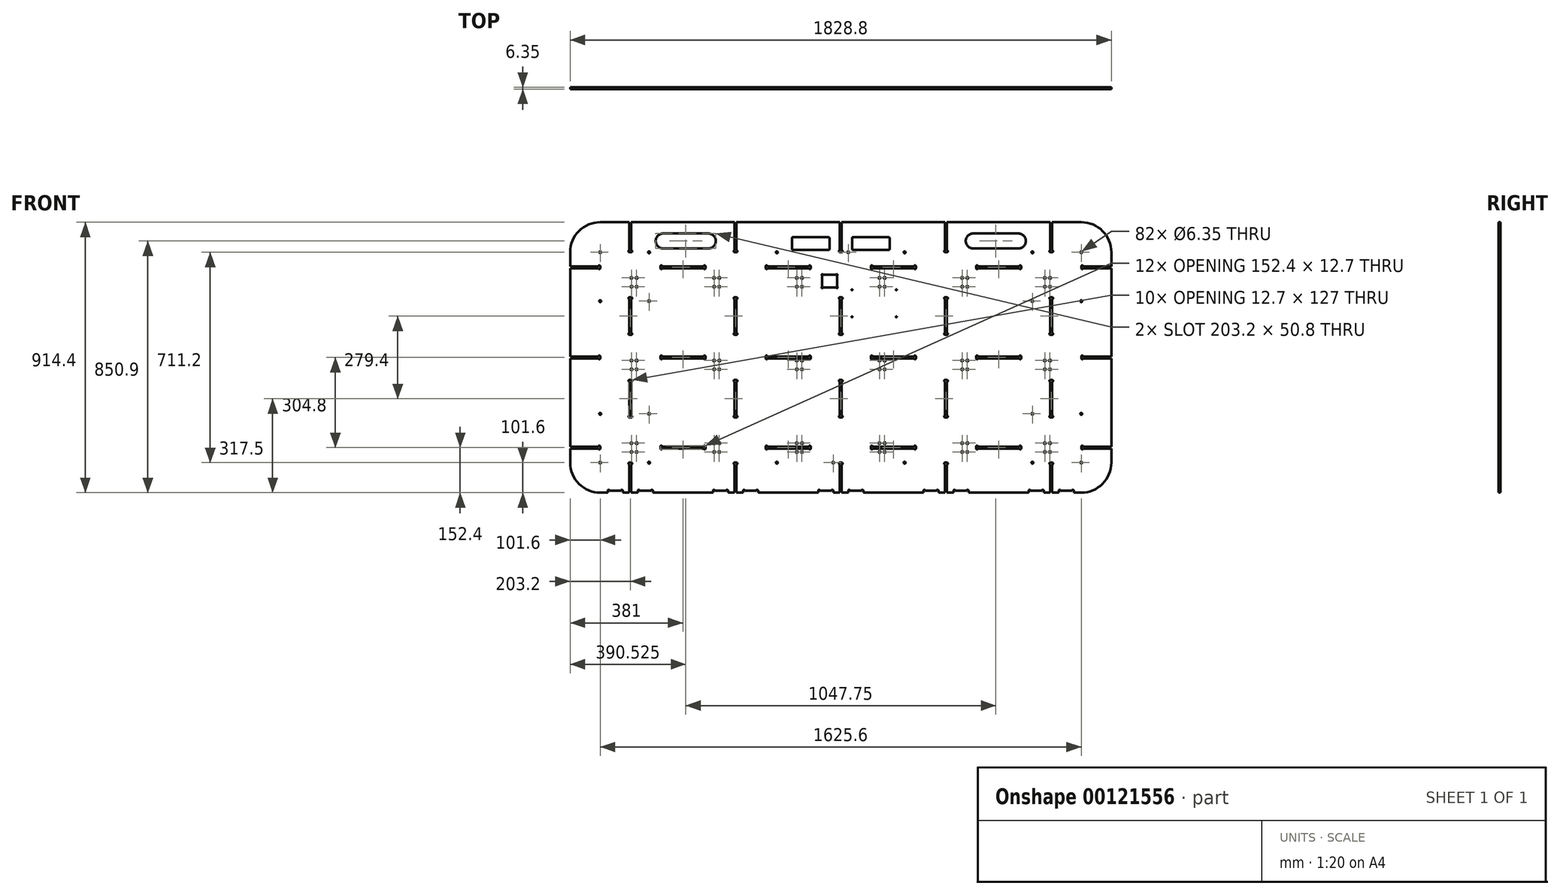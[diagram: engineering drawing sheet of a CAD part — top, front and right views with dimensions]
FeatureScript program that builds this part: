
annotation { "Feature Type Name" : "Feature", "Feature Type Description" : "" }
export const myFeature = defineFeature(function(context is Context, id is Id, definition is map)
    precondition{}
    {
        {
            var Q0;
            Q0=qCreatedBy(makeId("Front.planeOp"),FACE);
            var sketch = newSketch(context, id + "F0", { "sketchPlane" : qUnion([Q0])});
            skLineSegment(sketch, "E0.bottom", {"start": v(-812.8, 0) * mm, "end": v(812.8, 0) * mm});
            skLineSegment(sketch, "E0.top", {"start": v(-812.8, 914.4) * mm, "end": v(812.8, 914.4) * mm});
            skLineSegment(sketch, "E0.left", {"start": v(-914.4, 101.6) * mm, "end": v(-914.4, 812.8) * mm});
            skLineSegment(sketch, "E0.right", {"start": v(914.4, 101.6) * mm, "end": v(914.4, 812.8) * mm});
            skPoint(sketch, "E1.visualSharp", {"position": v(-914.4, 914.4) * mm});
            skArc(sketch, "E1.filletArc", {"start": v(-812.8, 914.4) * mm, "mid": v(-884.64, 884.64) * mm, "end": v(-914.4, 812.8) * mm});
            skPoint(sketch, "E2.visualSharp", {"position": v(-914.4, 0) * mm});
            skArc(sketch, "E2.filletArc", {"start": v(-914.4, 101.6) * mm, "mid": v(-884.64, 29.76) * mm, "end": v(-812.8, 0) * mm});
            skPoint(sketch, "E3.visualSharp", {"position": v(914.4, 0) * mm});
            skArc(sketch, "E3.filletArc", {"start": v(812.8, 0) * mm, "mid": v(884.64, 29.76) * mm, "end": v(914.4, 101.6) * mm});
            skPoint(sketch, "E4.visualSharp", {"position": v(914.4, 914.4) * mm});
            skArc(sketch, "E4.filletArc", {"start": v(914.4, 812.8) * mm, "mid": v(884.64, 884.64) * mm, "end": v(812.8, 914.4) * mm});
            skSolve(sketch);
        }
        {
            var Q0;
            Q0 = qSketchRegion(id + "F0", true);
            extrude(context, id + "F1", {"entities" : qUnion([Q0]), "depth" : 6.35 * mm});
        }
        {
            var Q0;
            Q0=makeQuery(id+"F1.opExtrude","CAP_FACE",FACE,{"disambiguationData":[OSD([sQuery(id+"F0.wireOp",EDGE,"E0.bottom"),sQuery(id+"F0.wireOp",EDGE,"E0.top"),sQuery(id+"F0.wireOp",EDGE,"E0.left"),sQuery(id+"F0.wireOp",EDGE,"E0.right"),sQuery(id+"F0.wireOp",EDGE,"E1.filletArc"),sQuery(id+"F0.wireOp",EDGE,"E2.filletArc"),sQuery(id+"F0.wireOp",EDGE,"E3.filletArc"),sQuery(id+"F0.wireOp",EDGE,"E4.filletArc")])],"isStart":false});
            var sketch = newSketch(context, id + "F2", { "sketchPlane" : qUnion([Q0])});
            skLineSegment(sketch, "E5", {"start": v(-711.2, 0) * mm, "end": v(-711.2, 914.4) * mm, "construction": true});
            skLineSegment(sketch, "E6", {"start": v(-711.2, 914.4) * mm, "end": v(-355.6, 914.4) * mm, "construction": true});
            skLineSegment(sketch, "E7", {"start": v(-355.6, 914.4) * mm, "end": v(-355.6, 0) * mm, "construction": true});
            skLineSegment(sketch, "E8", {"start": v(-355.6, 0) * mm, "end": v(0, 0) * mm, "construction": true});
            skLineSegment(sketch, "E9", {"start": v(0, 0) * mm, "end": v(0, 914.4) * mm, "construction": true});
            skPoint(sketch, "E9.endSnap0", {"position": v(0, 914.4) * mm});
            skLineSegment(sketch, "E10", {"start": v(0, 914.4) * mm, "end": v(355.6, 914.4) * mm, "construction": true});
            skLineSegment(sketch, "E11", {"start": v(355.6, 914.4) * mm, "end": v(355.6, 0) * mm, "construction": true});
            skLineSegment(sketch, "E12", {"start": v(355.6, 0) * mm, "end": v(711.2, 0) * mm, "construction": true});
            skLineSegment(sketch, "E13", {"start": v(711.2, 0) * mm, "end": v(711.2, 914.4) * mm, "construction": true});
            skLineSegment(sketch, "E14", {"start": v(-914.4, 762) * mm, "end": v(914.4, 762) * mm, "construction": true});
            skLineSegment(sketch, "E15", {"start": v(914.4, 762) * mm, "end": v(914.4, 457.2) * mm, "construction": true});
            skLineSegment(sketch, "E16", {"start": v(914.4, 457.2) * mm, "end": v(-914.4, 457.2) * mm, "construction": true});
            skLineSegment(sketch, "E17", {"start": v(-914.4, 457.2) * mm, "end": v(-914.4, 152.4) * mm, "construction": true});
            skLineSegment(sketch, "E18", {"start": v(-914.4, 152.4) * mm, "end": v(914.4, 152.4) * mm, "construction": true});
            skLineSegment(sketch, "E19", {"start": v(-714.38, 933.45) * mm, "end": v(-714.38, 933.45) * mm});
            skLineSegment(sketch, "E20", {"start": v(-714.38, 933.45) * mm, "end": v(-714.38, 819.15) * mm});
            skLineSegment(sketch, "E21", {"start": v(-714.38, 819.15) * mm, "end": v(-714.38, 819.15) * mm});
            skLineSegment(sketch, "E22", {"start": v(-714.38, 812.8) * mm, "end": v(-708.03, 812.8) * mm});
            skLineSegment(sketch, "E23", {"start": v(-708.03, 819.15) * mm, "end": v(-708.03, 819.15) * mm});
            skLineSegment(sketch, "E24", {"start": v(-708.03, 819.15) * mm, "end": v(-708.03, 933.45) * mm});
            skLineSegment(sketch, "E25", {"start": v(-708.03, 933.45) * mm, "end": v(-708.03, 933.45) * mm});
            skLineSegment(sketch, "E26", {"start": v(-708.03, 939.8) * mm, "end": v(-714.37, 939.8) * mm});
            skArc(sketch, "E27", {"start": v(-708.03, 939.8) * mm, "mid": v(-704.85, 936.63) * mm, "end": v(-708.03, 933.45) * mm});
            skArc(sketch, "E28", {"start": v(-714.37, 939.8) * mm, "mid": v(-717.55, 936.63) * mm, "end": v(-714.38, 933.45) * mm});
            skArc(sketch, "E29", {"start": v(-714.38, 819.15) * mm, "mid": v(-717.55, 815.97) * mm, "end": v(-714.38, 812.8) * mm});
            skArc(sketch, "E30", {"start": v(-708.03, 819.15) * mm, "mid": v(-704.85, 815.97) * mm, "end": v(-708.03, 812.8) * mm});
            skLineSegment(sketch, "E31.0.1.0", {"start": v(-708.03, 660.4) * mm, "end": v(-714.38, 660.4) * mm});
            skArc(sketch, "E31.0.1.1", {"start": v(-714.38, 660.4) * mm, "mid": v(-717.55, 657.23) * mm, "end": v(-714.38, 654.05) * mm});
            skLineSegment(sketch, "E31.0.1.2", {"start": v(-714.38, 654.05) * mm, "end": v(-714.38, 539.75) * mm});
            skArc(sketch, "E31.0.1.3", {"start": v(-708.03, 660.4) * mm, "mid": v(-704.85, 657.23) * mm, "end": v(-708.03, 654.05) * mm});
            skLineSegment(sketch, "E31.0.1.4", {"start": v(-708.03, 539.75) * mm, "end": v(-708.03, 654.05) * mm});
            skArc(sketch, "E31.0.1.5", {"start": v(-714.38, 539.75) * mm, "mid": v(-717.55, 536.58) * mm, "end": v(-714.38, 533.4) * mm});
            skLineSegment(sketch, "E31.0.1.6", {"start": v(-714.38, 533.4) * mm, "end": v(-708.03, 533.4) * mm});
            skArc(sketch, "E31.0.1.7", {"start": v(-708.03, 539.75) * mm, "mid": v(-704.85, 536.58) * mm, "end": v(-708.03, 533.4) * mm});
            skLineSegment(sketch, "E31.0.2.0", {"start": v(-708.03, 381) * mm, "end": v(-714.38, 381) * mm});
            skArc(sketch, "E31.0.2.1", {"start": v(-714.38, 381) * mm, "mid": v(-717.55, 377.83) * mm, "end": v(-714.37, 374.65) * mm});
            skLineSegment(sketch, "E31.0.2.2", {"start": v(-714.38, 374.65) * mm, "end": v(-714.38, 260.35) * mm});
            skArc(sketch, "E31.0.2.3", {"start": v(-708.03, 381) * mm, "mid": v(-704.85, 377.83) * mm, "end": v(-708.03, 374.65) * mm});
            skLineSegment(sketch, "E31.0.2.4", {"start": v(-708.03, 260.35) * mm, "end": v(-708.03, 374.65) * mm});
            skArc(sketch, "E31.0.2.5", {"start": v(-714.37, 260.35) * mm, "mid": v(-717.55, 257.18) * mm, "end": v(-714.38, 254) * mm});
            skLineSegment(sketch, "E31.0.2.6", {"start": v(-714.38, 254) * mm, "end": v(-708.03, 254) * mm});
            skArc(sketch, "E31.0.2.7", {"start": v(-708.03, 260.35) * mm, "mid": v(-704.85, 257.18) * mm, "end": v(-708.03, 254) * mm});
            skLineSegment(sketch, "E31.0.3.0", {"start": v(-708.03, 101.6) * mm, "end": v(-714.38, 101.6) * mm});
            skArc(sketch, "E31.0.3.1", {"start": v(-714.38, 101.6) * mm, "mid": v(-717.55, 98.43) * mm, "end": v(-714.37, 95.25) * mm});
            skLineSegment(sketch, "E31.0.3.2", {"start": v(-714.38, 95.25) * mm, "end": v(-714.38, -19.05) * mm});
            skArc(sketch, "E31.0.3.3", {"start": v(-708.03, 101.6) * mm, "mid": v(-704.85, 98.43) * mm, "end": v(-708.03, 95.25) * mm});
            skLineSegment(sketch, "E31.0.3.4", {"start": v(-708.03, -19.05) * mm, "end": v(-708.03, 95.25) * mm});
            skArc(sketch, "E31.0.3.5", {"start": v(-714.37, -19.05) * mm, "mid": v(-717.55, -22.22) * mm, "end": v(-714.38, -25.4) * mm});
            skLineSegment(sketch, "E31.0.3.6", {"start": v(-714.38, -25.4) * mm, "end": v(-708.03, -25.4) * mm});
            skArc(sketch, "E31.0.3.7", {"start": v(-708.03, -19.05) * mm, "mid": v(-704.85, -22.22) * mm, "end": v(-708.03, -25.4) * mm});
            skLineSegment(sketch, "E31.1.0.0", {"start": v(-352.43, 939.8) * mm, "end": v(-358.77, 939.8) * mm});
            skArc(sketch, "E31.1.0.1", {"start": v(-358.77, 939.8) * mm, "mid": v(-361.95, 936.63) * mm, "end": v(-358.77, 933.45) * mm});
            skLineSegment(sketch, "E31.1.0.2", {"start": v(-358.77, 933.45) * mm, "end": v(-358.77, 819.15) * mm});
            skArc(sketch, "E31.1.0.3", {"start": v(-352.43, 939.8) * mm, "mid": v(-349.25, 936.63) * mm, "end": v(-352.43, 933.45) * mm});
            skLineSegment(sketch, "E31.1.0.4", {"start": v(-352.43, 819.15) * mm, "end": v(-352.43, 933.45) * mm});
            skArc(sketch, "E31.1.0.5", {"start": v(-358.77, 819.15) * mm, "mid": v(-361.95, 815.97) * mm, "end": v(-358.77, 812.8) * mm});
            skLineSegment(sketch, "E31.1.0.6", {"start": v(-358.77, 812.8) * mm, "end": v(-352.43, 812.8) * mm});
            skArc(sketch, "E31.1.0.7", {"start": v(-352.43, 819.15) * mm, "mid": v(-349.25, 815.97) * mm, "end": v(-352.43, 812.8) * mm});
            skLineSegment(sketch, "E31.1.1.0", {"start": v(-352.43, 660.4) * mm, "end": v(-358.77, 660.4) * mm});
            skArc(sketch, "E31.1.1.1", {"start": v(-358.77, 660.4) * mm, "mid": v(-361.95, 657.23) * mm, "end": v(-358.77, 654.05) * mm});
            skLineSegment(sketch, "E31.1.1.2", {"start": v(-358.77, 654.05) * mm, "end": v(-358.77, 539.75) * mm});
            skArc(sketch, "E31.1.1.3", {"start": v(-352.43, 660.4) * mm, "mid": v(-349.25, 657.23) * mm, "end": v(-352.43, 654.05) * mm});
            skLineSegment(sketch, "E31.1.1.4", {"start": v(-352.43, 539.75) * mm, "end": v(-352.43, 654.05) * mm});
            skArc(sketch, "E31.1.1.5", {"start": v(-358.77, 539.75) * mm, "mid": v(-361.95, 536.58) * mm, "end": v(-358.77, 533.4) * mm});
            skLineSegment(sketch, "E31.1.1.6", {"start": v(-358.77, 533.4) * mm, "end": v(-352.43, 533.4) * mm});
            skArc(sketch, "E31.1.1.7", {"start": v(-352.43, 539.75) * mm, "mid": v(-349.25, 536.58) * mm, "end": v(-352.43, 533.4) * mm});
            skLineSegment(sketch, "E31.1.2.0", {"start": v(-352.43, 381) * mm, "end": v(-358.77, 381) * mm});
            skArc(sketch, "E31.1.2.1", {"start": v(-358.77, 381) * mm, "mid": v(-361.95, 377.83) * mm, "end": v(-358.77, 374.65) * mm});
            skLineSegment(sketch, "E31.1.2.2", {"start": v(-358.77, 374.65) * mm, "end": v(-358.77, 260.35) * mm});
            skArc(sketch, "E31.1.2.3", {"start": v(-352.43, 381) * mm, "mid": v(-349.25, 377.83) * mm, "end": v(-352.43, 374.65) * mm});
            skLineSegment(sketch, "E31.1.2.4", {"start": v(-352.43, 260.35) * mm, "end": v(-352.43, 374.65) * mm});
            skArc(sketch, "E31.1.2.5", {"start": v(-358.77, 260.35) * mm, "mid": v(-361.95, 257.18) * mm, "end": v(-358.77, 254) * mm});
            skLineSegment(sketch, "E31.1.2.6", {"start": v(-358.77, 254) * mm, "end": v(-352.43, 254) * mm});
            skArc(sketch, "E31.1.2.7", {"start": v(-352.43, 260.35) * mm, "mid": v(-349.25, 257.18) * mm, "end": v(-352.43, 254) * mm});
            skLineSegment(sketch, "E31.1.3.0", {"start": v(-352.43, 101.6) * mm, "end": v(-358.77, 101.6) * mm});
            skArc(sketch, "E31.1.3.1", {"start": v(-358.77, 101.6) * mm, "mid": v(-361.95, 98.43) * mm, "end": v(-358.77, 95.25) * mm});
            skLineSegment(sketch, "E31.1.3.2", {"start": v(-358.77, 95.25) * mm, "end": v(-358.77, -19.05) * mm});
            skArc(sketch, "E31.1.3.3", {"start": v(-352.43, 101.6) * mm, "mid": v(-349.25, 98.43) * mm, "end": v(-352.43, 95.25) * mm});
            skLineSegment(sketch, "E31.1.3.4", {"start": v(-352.43, -19.05) * mm, "end": v(-352.43, 95.25) * mm});
            skArc(sketch, "E31.1.3.5", {"start": v(-358.77, -19.05) * mm, "mid": v(-361.95, -22.22) * mm, "end": v(-358.77, -25.4) * mm});
            skLineSegment(sketch, "E31.1.3.6", {"start": v(-358.77, -25.4) * mm, "end": v(-352.43, -25.4) * mm});
            skArc(sketch, "E31.1.3.7", {"start": v(-352.43, -19.05) * mm, "mid": v(-349.25, -22.22) * mm, "end": v(-352.43, -25.4) * mm});
            skLineSegment(sketch, "E31.2.0.0", {"start": v(3.17, 939.8) * mm, "end": v(-3.17, 939.8) * mm});
            skArc(sketch, "E31.2.0.1", {"start": v(-3.17, 939.8) * mm, "mid": v(-6.35, 936.63) * mm, "end": v(-3.17, 933.45) * mm});
            skLineSegment(sketch, "E31.2.0.2", {"start": v(-3.17, 933.45) * mm, "end": v(-3.17, 819.15) * mm});
            skArc(sketch, "E31.2.0.3", {"start": v(3.17, 939.8) * mm, "mid": v(6.35, 936.63) * mm, "end": v(3.17, 933.45) * mm});
            skLineSegment(sketch, "E31.2.0.4", {"start": v(3.17, 819.15) * mm, "end": v(3.17, 933.45) * mm});
            skArc(sketch, "E31.2.0.5", {"start": v(-3.17, 819.15) * mm, "mid": v(-6.35, 815.97) * mm, "end": v(-3.17, 812.8) * mm});
            skLineSegment(sketch, "E31.2.0.6", {"start": v(-3.17, 812.8) * mm, "end": v(3.17, 812.8) * mm});
            skArc(sketch, "E31.2.0.7", {"start": v(3.17, 819.15) * mm, "mid": v(6.35, 815.97) * mm, "end": v(3.17, 812.8) * mm});
            skLineSegment(sketch, "E31.2.1.0", {"start": v(3.17, 660.4) * mm, "end": v(-3.17, 660.4) * mm});
            skArc(sketch, "E31.2.1.1", {"start": v(-3.17, 660.4) * mm, "mid": v(-6.35, 657.23) * mm, "end": v(-3.17, 654.05) * mm});
            skLineSegment(sketch, "E31.2.1.2", {"start": v(-3.17, 654.05) * mm, "end": v(-3.17, 539.75) * mm});
            skArc(sketch, "E31.2.1.3", {"start": v(3.17, 660.4) * mm, "mid": v(6.35, 657.23) * mm, "end": v(3.17, 654.05) * mm});
            skLineSegment(sketch, "E31.2.1.4", {"start": v(3.17, 539.75) * mm, "end": v(3.17, 654.05) * mm});
            skArc(sketch, "E31.2.1.5", {"start": v(-3.17, 539.75) * mm, "mid": v(-6.35, 536.58) * mm, "end": v(-3.17, 533.4) * mm});
            skLineSegment(sketch, "E31.2.1.6", {"start": v(-3.17, 533.4) * mm, "end": v(3.17, 533.4) * mm});
            skArc(sketch, "E31.2.1.7", {"start": v(3.17, 539.75) * mm, "mid": v(6.35, 536.58) * mm, "end": v(3.17, 533.4) * mm});
            skLineSegment(sketch, "E31.2.2.0", {"start": v(3.17, 381) * mm, "end": v(-3.17, 381) * mm});
            skArc(sketch, "E31.2.2.1", {"start": v(-3.17, 381) * mm, "mid": v(-6.35, 377.83) * mm, "end": v(-3.17, 374.65) * mm});
            skLineSegment(sketch, "E31.2.2.2", {"start": v(-3.17, 374.65) * mm, "end": v(-3.17, 260.35) * mm});
            skArc(sketch, "E31.2.2.3", {"start": v(3.17, 381) * mm, "mid": v(6.35, 377.83) * mm, "end": v(3.17, 374.65) * mm});
            skLineSegment(sketch, "E31.2.2.4", {"start": v(3.17, 260.35) * mm, "end": v(3.17, 374.65) * mm});
            skArc(sketch, "E31.2.2.5", {"start": v(-3.17, 260.35) * mm, "mid": v(-6.35, 257.18) * mm, "end": v(-3.17, 254) * mm});
            skLineSegment(sketch, "E31.2.2.6", {"start": v(-3.17, 254) * mm, "end": v(3.17, 254) * mm});
            skArc(sketch, "E31.2.2.7", {"start": v(3.17, 260.35) * mm, "mid": v(6.35, 257.18) * mm, "end": v(3.17, 254) * mm});
            skLineSegment(sketch, "E31.2.3.0", {"start": v(3.17, 101.6) * mm, "end": v(-3.17, 101.6) * mm});
            skArc(sketch, "E31.2.3.1", {"start": v(-3.17, 101.6) * mm, "mid": v(-6.35, 98.43) * mm, "end": v(-3.17, 95.25) * mm});
            skLineSegment(sketch, "E31.2.3.2", {"start": v(-3.17, 95.25) * mm, "end": v(-3.17, -19.05) * mm});
            skArc(sketch, "E31.2.3.3", {"start": v(3.17, 101.6) * mm, "mid": v(6.35, 98.43) * mm, "end": v(3.17, 95.25) * mm});
            skLineSegment(sketch, "E31.2.3.4", {"start": v(3.17, -19.05) * mm, "end": v(3.17, 95.25) * mm});
            skArc(sketch, "E31.2.3.5", {"start": v(-3.17, -19.05) * mm, "mid": v(-6.35, -22.22) * mm, "end": v(-3.17, -25.4) * mm});
            skLineSegment(sketch, "E31.2.3.6", {"start": v(-3.17, -25.4) * mm, "end": v(3.17, -25.4) * mm});
            skArc(sketch, "E31.2.3.7", {"start": v(3.17, -19.05) * mm, "mid": v(6.35, -22.22) * mm, "end": v(3.17, -25.4) * mm});
            skLineSegment(sketch, "E31.3.0.0", {"start": v(358.77, 939.8) * mm, "end": v(352.43, 939.8) * mm});
            skArc(sketch, "E31.3.0.1", {"start": v(352.43, 939.8) * mm, "mid": v(349.25, 936.63) * mm, "end": v(352.43, 933.45) * mm});
            skLineSegment(sketch, "E31.3.0.2", {"start": v(352.43, 933.45) * mm, "end": v(352.43, 819.15) * mm});
            skArc(sketch, "E31.3.0.3", {"start": v(358.77, 939.8) * mm, "mid": v(361.95, 936.63) * mm, "end": v(358.77, 933.45) * mm});
            skLineSegment(sketch, "E31.3.0.4", {"start": v(358.77, 819.15) * mm, "end": v(358.77, 933.45) * mm});
            skArc(sketch, "E31.3.0.5", {"start": v(352.43, 819.15) * mm, "mid": v(349.25, 815.97) * mm, "end": v(352.43, 812.8) * mm});
            skLineSegment(sketch, "E31.3.0.6", {"start": v(352.43, 812.8) * mm, "end": v(358.77, 812.8) * mm});
            skArc(sketch, "E31.3.0.7", {"start": v(358.77, 819.15) * mm, "mid": v(361.95, 815.97) * mm, "end": v(358.77, 812.8) * mm});
            skLineSegment(sketch, "E31.3.1.0", {"start": v(358.77, 660.4) * mm, "end": v(352.43, 660.4) * mm});
            skArc(sketch, "E31.3.1.1", {"start": v(352.43, 660.4) * mm, "mid": v(349.25, 657.23) * mm, "end": v(352.43, 654.05) * mm});
            skLineSegment(sketch, "E31.3.1.2", {"start": v(352.43, 654.05) * mm, "end": v(352.43, 539.75) * mm});
            skArc(sketch, "E31.3.1.3", {"start": v(358.77, 660.4) * mm, "mid": v(361.95, 657.23) * mm, "end": v(358.77, 654.05) * mm});
            skLineSegment(sketch, "E31.3.1.4", {"start": v(358.77, 539.75) * mm, "end": v(358.77, 654.05) * mm});
            skArc(sketch, "E31.3.1.5", {"start": v(352.43, 539.75) * mm, "mid": v(349.25, 536.58) * mm, "end": v(352.43, 533.4) * mm});
            skLineSegment(sketch, "E31.3.1.6", {"start": v(352.43, 533.4) * mm, "end": v(358.77, 533.4) * mm});
            skArc(sketch, "E31.3.1.7", {"start": v(358.77, 539.75) * mm, "mid": v(361.95, 536.58) * mm, "end": v(358.77, 533.4) * mm});
            skLineSegment(sketch, "E31.3.2.0", {"start": v(358.77, 381) * mm, "end": v(352.43, 381) * mm});
            skArc(sketch, "E31.3.2.1", {"start": v(352.43, 381) * mm, "mid": v(349.25, 377.83) * mm, "end": v(352.43, 374.65) * mm});
            skLineSegment(sketch, "E31.3.2.2", {"start": v(352.43, 374.65) * mm, "end": v(352.43, 260.35) * mm});
            skArc(sketch, "E31.3.2.3", {"start": v(358.77, 381) * mm, "mid": v(361.95, 377.83) * mm, "end": v(358.77, 374.65) * mm});
            skLineSegment(sketch, "E31.3.2.4", {"start": v(358.77, 260.35) * mm, "end": v(358.77, 374.65) * mm});
            skArc(sketch, "E31.3.2.5", {"start": v(352.43, 260.35) * mm, "mid": v(349.25, 257.18) * mm, "end": v(352.43, 254) * mm});
            skLineSegment(sketch, "E31.3.2.6", {"start": v(352.43, 254) * mm, "end": v(358.77, 254) * mm});
            skArc(sketch, "E31.3.2.7", {"start": v(358.77, 260.35) * mm, "mid": v(361.95, 257.18) * mm, "end": v(358.77, 254) * mm});
            skLineSegment(sketch, "E31.3.3.0", {"start": v(358.77, 101.6) * mm, "end": v(352.43, 101.6) * mm});
            skArc(sketch, "E31.3.3.1", {"start": v(352.43, 101.6) * mm, "mid": v(349.25, 98.43) * mm, "end": v(352.43, 95.25) * mm});
            skLineSegment(sketch, "E31.3.3.2", {"start": v(352.43, 95.25) * mm, "end": v(352.43, -19.05) * mm});
            skArc(sketch, "E31.3.3.3", {"start": v(358.77, 101.6) * mm, "mid": v(361.95, 98.43) * mm, "end": v(358.77, 95.25) * mm});
            skLineSegment(sketch, "E31.3.3.4", {"start": v(358.77, -19.05) * mm, "end": v(358.77, 95.25) * mm});
            skArc(sketch, "E31.3.3.5", {"start": v(352.43, -19.05) * mm, "mid": v(349.25, -22.22) * mm, "end": v(352.43, -25.4) * mm});
            skLineSegment(sketch, "E31.3.3.6", {"start": v(352.43, -25.4) * mm, "end": v(358.77, -25.4) * mm});
            skArc(sketch, "E31.3.3.7", {"start": v(358.77, -19.05) * mm, "mid": v(361.95, -22.22) * mm, "end": v(358.77, -25.4) * mm});
            skLineSegment(sketch, "E31.4.0.0", {"start": v(714.38, 939.8) * mm, "end": v(708.03, 939.8) * mm});
            skArc(sketch, "E31.4.0.1", {"start": v(708.03, 939.8) * mm, "mid": v(704.85, 936.63) * mm, "end": v(708.03, 933.45) * mm});
            skLineSegment(sketch, "E31.4.0.2", {"start": v(708.03, 933.45) * mm, "end": v(708.03, 819.15) * mm});
            skArc(sketch, "E31.4.0.3", {"start": v(714.38, 939.8) * mm, "mid": v(717.55, 936.63) * mm, "end": v(714.38, 933.45) * mm});
            skLineSegment(sketch, "E31.4.0.4", {"start": v(714.38, 819.15) * mm, "end": v(714.38, 933.45) * mm});
            skArc(sketch, "E31.4.0.5", {"start": v(708.03, 819.15) * mm, "mid": v(704.85, 815.97) * mm, "end": v(708.03, 812.8) * mm});
            skLineSegment(sketch, "E31.4.0.6", {"start": v(708.03, 812.8) * mm, "end": v(714.38, 812.8) * mm});
            skArc(sketch, "E31.4.0.7", {"start": v(714.38, 819.15) * mm, "mid": v(717.55, 815.97) * mm, "end": v(714.38, 812.8) * mm});
            skLineSegment(sketch, "E31.4.1.0", {"start": v(714.38, 660.4) * mm, "end": v(708.03, 660.4) * mm});
            skArc(sketch, "E31.4.1.1", {"start": v(708.03, 660.4) * mm, "mid": v(704.85, 657.23) * mm, "end": v(708.03, 654.05) * mm});
            skLineSegment(sketch, "E31.4.1.2", {"start": v(708.03, 654.05) * mm, "end": v(708.03, 539.75) * mm});
            skArc(sketch, "E31.4.1.3", {"start": v(714.38, 660.4) * mm, "mid": v(717.55, 657.23) * mm, "end": v(714.38, 654.05) * mm});
            skLineSegment(sketch, "E31.4.1.4", {"start": v(714.38, 539.75) * mm, "end": v(714.38, 654.05) * mm});
            skArc(sketch, "E31.4.1.5", {"start": v(708.03, 539.75) * mm, "mid": v(704.85, 536.58) * mm, "end": v(708.03, 533.4) * mm});
            skLineSegment(sketch, "E31.4.1.6", {"start": v(708.03, 533.4) * mm, "end": v(714.38, 533.4) * mm});
            skArc(sketch, "E31.4.1.7", {"start": v(714.38, 539.75) * mm, "mid": v(717.55, 536.58) * mm, "end": v(714.38, 533.4) * mm});
            skLineSegment(sketch, "E31.4.2.0", {"start": v(714.38, 381) * mm, "end": v(708.03, 381) * mm});
            skArc(sketch, "E31.4.2.1", {"start": v(708.03, 381) * mm, "mid": v(704.85, 377.83) * mm, "end": v(708.03, 374.65) * mm});
            skLineSegment(sketch, "E31.4.2.2", {"start": v(708.03, 374.65) * mm, "end": v(708.03, 260.35) * mm});
            skArc(sketch, "E31.4.2.3", {"start": v(714.38, 381) * mm, "mid": v(717.55, 377.83) * mm, "end": v(714.38, 374.65) * mm});
            skLineSegment(sketch, "E31.4.2.4", {"start": v(714.38, 260.35) * mm, "end": v(714.38, 374.65) * mm});
            skArc(sketch, "E31.4.2.5", {"start": v(708.03, 260.35) * mm, "mid": v(704.85, 257.18) * mm, "end": v(708.03, 254) * mm});
            skLineSegment(sketch, "E31.4.2.6", {"start": v(708.03, 254) * mm, "end": v(714.38, 254) * mm});
            skArc(sketch, "E31.4.2.7", {"start": v(714.38, 260.35) * mm, "mid": v(717.55, 257.18) * mm, "end": v(714.38, 254) * mm});
            skLineSegment(sketch, "E31.4.3.0", {"start": v(714.38, 101.6) * mm, "end": v(708.03, 101.6) * mm});
            skArc(sketch, "E31.4.3.1", {"start": v(708.03, 101.6) * mm, "mid": v(704.85, 98.43) * mm, "end": v(708.03, 95.25) * mm});
            skLineSegment(sketch, "E31.4.3.2", {"start": v(708.03, 95.25) * mm, "end": v(708.03, -19.05) * mm});
            skArc(sketch, "E31.4.3.3", {"start": v(714.38, 101.6) * mm, "mid": v(717.55, 98.43) * mm, "end": v(714.38, 95.25) * mm});
            skLineSegment(sketch, "E31.4.3.4", {"start": v(714.38, -19.05) * mm, "end": v(714.38, 95.25) * mm});
            skArc(sketch, "E31.4.3.5", {"start": v(708.03, -19.05) * mm, "mid": v(704.85, -22.22) * mm, "end": v(708.03, -25.4) * mm});
            skLineSegment(sketch, "E31.4.3.6", {"start": v(708.03, -25.4) * mm, "end": v(714.38, -25.4) * mm});
            skArc(sketch, "E31.4.3.7", {"start": v(714.38, -19.05) * mm, "mid": v(717.55, -22.22) * mm, "end": v(714.38, -25.4) * mm});
            skLineSegment(sketch, "E31.direction1", {"start": v(-714.38, 812.8) * mm, "end": v(-358.77, 812.8) * mm, "construction": true});
            skLineSegment(sketch, "E31.direction2", {"start": v(-714.38, 812.8) * mm, "end": v(-714.38, 533.4) * mm, "construction": true});
            skPoint(sketch, "E32", {"position": v(-711.2, 812.8) * mm});
            skPoint(sketch, "E33", {"position": v(-914.4, 457.2) * mm});
            skSolve(sketch);
        }
        {
            var Q0;
            Q0 = qSketchRegion(id + "F2", true);
            extrude(context, id + "F3", {"entities" : qUnion([Q0]), "operationType" : NewBodyOperationType.REMOVE, "endBound" : BoundingType.THROUGH_ALL, "oppositeDirection" : true, "depth" : 25.4 * mm});
        }
        {
            var Q0;
            Q0=makeQuery(id+"F1.opExtrude","CAP_FACE",FACE,{"disambiguationData":[OSD([sQuery(id+"F0.wireOp",EDGE,"E0.bottom"),sQuery(id+"F0.wireOp",EDGE,"E0.top"),sQuery(id+"F0.wireOp",EDGE,"E0.left"),sQuery(id+"F0.wireOp",EDGE,"E0.right"),sQuery(id+"F0.wireOp",EDGE,"E1.filletArc"),sQuery(id+"F0.wireOp",EDGE,"E2.filletArc"),sQuery(id+"F0.wireOp",EDGE,"E3.filletArc"),sQuery(id+"F0.wireOp",EDGE,"E4.filletArc")])],"isStart":false});
            var sketch = newSketch(context, id + "F4", { "sketchPlane" : qUnion([Q0])});
            skLineSegment(sketch, "E34", {"start": v(-958.85, 765.17) * mm, "end": v(-819.15, 765.17) * mm});
            skLineSegment(sketch, "E35", {"start": v(-958.85, 758.83) * mm, "end": v(-819.15, 758.83) * mm});
            skLineSegment(sketch, "E36", {"start": v(-965.2, 765.17) * mm, "end": v(-965.2, 758.83) * mm});
            skLineSegment(sketch, "E37", {"start": v(-812.8, 765.17) * mm, "end": v(-812.8, 758.83) * mm});
            skArc(sketch, "E38", {"start": v(-958.85, 765.17) * mm, "mid": v(-962.03, 768.35) * mm, "end": v(-965.2, 765.17) * mm});
            skArc(sketch, "E39", {"start": v(-965.2, 758.83) * mm, "mid": v(-962.03, 755.65) * mm, "end": v(-958.85, 758.83) * mm});
            skArc(sketch, "E40", {"start": v(-812.8, 765.17) * mm, "mid": v(-815.97, 768.35) * mm, "end": v(-819.15, 765.17) * mm});
            skArc(sketch, "E41", {"start": v(-819.15, 758.83) * mm, "mid": v(-815.97, 755.65) * mm, "end": v(-812.8, 758.83) * mm});
            skArc(sketch, "E42.0.1.0", {"start": v(-958.85, 460.38) * mm, "mid": v(-962.03, 463.55) * mm, "end": v(-965.2, 460.38) * mm});
            skLineSegment(sketch, "E42.0.1.1", {"start": v(-965.2, 460.38) * mm, "end": v(-965.2, 454.03) * mm});
            skArc(sketch, "E42.0.1.2", {"start": v(-965.2, 454.03) * mm, "mid": v(-962.03, 450.85) * mm, "end": v(-958.85, 454.03) * mm});
            skLineSegment(sketch, "E42.0.1.3", {"start": v(-958.85, 454.03) * mm, "end": v(-819.15, 454.03) * mm});
            skLineSegment(sketch, "E42.0.1.4", {"start": v(-958.85, 460.38) * mm, "end": v(-819.15, 460.38) * mm});
            skArc(sketch, "E42.0.1.5", {"start": v(-812.8, 460.38) * mm, "mid": v(-815.97, 463.55) * mm, "end": v(-819.15, 460.38) * mm});
            skLineSegment(sketch, "E42.0.1.6", {"start": v(-812.8, 460.38) * mm, "end": v(-812.8, 454.03) * mm});
            skArc(sketch, "E42.0.1.7", {"start": v(-819.15, 454.03) * mm, "mid": v(-815.97, 450.85) * mm, "end": v(-812.8, 454.03) * mm});
            skArc(sketch, "E42.0.2.0", {"start": v(-958.85, 155.58) * mm, "mid": v(-962.03, 158.75) * mm, "end": v(-965.2, 155.58) * mm});
            skLineSegment(sketch, "E42.0.2.1", {"start": v(-965.2, 155.58) * mm, "end": v(-965.2, 149.23) * mm});
            skArc(sketch, "E42.0.2.2", {"start": v(-965.2, 149.23) * mm, "mid": v(-962.03, 146.05) * mm, "end": v(-958.85, 149.23) * mm});
            skLineSegment(sketch, "E42.0.2.3", {"start": v(-958.85, 149.23) * mm, "end": v(-819.15, 149.23) * mm});
            skLineSegment(sketch, "E42.0.2.4", {"start": v(-958.85, 155.58) * mm, "end": v(-819.15, 155.58) * mm});
            skArc(sketch, "E42.0.2.5", {"start": v(-812.8, 155.58) * mm, "mid": v(-815.97, 158.75) * mm, "end": v(-819.15, 155.58) * mm});
            skLineSegment(sketch, "E42.0.2.6", {"start": v(-812.8, 155.58) * mm, "end": v(-812.8, 149.23) * mm});
            skArc(sketch, "E42.0.2.7", {"start": v(-819.15, 149.23) * mm, "mid": v(-815.97, 146.05) * mm, "end": v(-812.8, 149.23) * mm});
            skArc(sketch, "E42.1.0.0", {"start": v(-603.25, 765.17) * mm, "mid": v(-606.43, 768.35) * mm, "end": v(-609.6, 765.17) * mm});
            skLineSegment(sketch, "E42.1.0.1", {"start": v(-609.6, 765.17) * mm, "end": v(-609.6, 758.83) * mm});
            skArc(sketch, "E42.1.0.2", {"start": v(-609.6, 758.83) * mm, "mid": v(-606.43, 755.65) * mm, "end": v(-603.25, 758.83) * mm});
            skLineSegment(sketch, "E42.1.0.3", {"start": v(-603.25, 758.83) * mm, "end": v(-463.55, 758.83) * mm});
            skLineSegment(sketch, "E42.1.0.4", {"start": v(-603.25, 765.17) * mm, "end": v(-463.55, 765.17) * mm});
            skArc(sketch, "E42.1.0.5", {"start": v(-457.2, 765.17) * mm, "mid": v(-460.37, 768.35) * mm, "end": v(-463.55, 765.17) * mm});
            skLineSegment(sketch, "E42.1.0.6", {"start": v(-457.2, 765.17) * mm, "end": v(-457.2, 758.83) * mm});
            skArc(sketch, "E42.1.0.7", {"start": v(-463.55, 758.83) * mm, "mid": v(-460.37, 755.65) * mm, "end": v(-457.2, 758.83) * mm});
            skArc(sketch, "E42.1.1.0", {"start": v(-603.25, 460.38) * mm, "mid": v(-606.43, 463.55) * mm, "end": v(-609.6, 460.38) * mm});
            skLineSegment(sketch, "E42.1.1.1", {"start": v(-609.6, 460.38) * mm, "end": v(-609.6, 454.03) * mm});
            skArc(sketch, "E42.1.1.2", {"start": v(-609.6, 454.03) * mm, "mid": v(-606.43, 450.85) * mm, "end": v(-603.25, 454.03) * mm});
            skLineSegment(sketch, "E42.1.1.3", {"start": v(-603.25, 454.03) * mm, "end": v(-463.55, 454.03) * mm});
            skLineSegment(sketch, "E42.1.1.4", {"start": v(-603.25, 460.38) * mm, "end": v(-463.55, 460.38) * mm});
            skArc(sketch, "E42.1.1.5", {"start": v(-457.2, 460.38) * mm, "mid": v(-460.37, 463.55) * mm, "end": v(-463.55, 460.38) * mm});
            skLineSegment(sketch, "E42.1.1.6", {"start": v(-457.2, 460.38) * mm, "end": v(-457.2, 454.03) * mm});
            skArc(sketch, "E42.1.1.7", {"start": v(-463.55, 454.03) * mm, "mid": v(-460.37, 450.85) * mm, "end": v(-457.2, 454.03) * mm});
            skArc(sketch, "E42.1.2.0", {"start": v(-603.25, 155.58) * mm, "mid": v(-606.43, 158.75) * mm, "end": v(-609.6, 155.58) * mm});
            skLineSegment(sketch, "E42.1.2.1", {"start": v(-609.6, 155.58) * mm, "end": v(-609.6, 149.23) * mm});
            skArc(sketch, "E42.1.2.2", {"start": v(-609.6, 149.23) * mm, "mid": v(-606.43, 146.05) * mm, "end": v(-603.25, 149.23) * mm});
            skLineSegment(sketch, "E42.1.2.3", {"start": v(-603.25, 149.23) * mm, "end": v(-463.55, 149.23) * mm});
            skLineSegment(sketch, "E42.1.2.4", {"start": v(-603.25, 155.58) * mm, "end": v(-463.55, 155.58) * mm});
            skArc(sketch, "E42.1.2.5", {"start": v(-457.2, 155.58) * mm, "mid": v(-460.37, 158.75) * mm, "end": v(-463.55, 155.58) * mm});
            skLineSegment(sketch, "E42.1.2.6", {"start": v(-457.2, 155.58) * mm, "end": v(-457.2, 149.23) * mm});
            skArc(sketch, "E42.1.2.7", {"start": v(-463.55, 149.23) * mm, "mid": v(-460.37, 146.05) * mm, "end": v(-457.2, 149.23) * mm});
            skArc(sketch, "E42.2.0.0", {"start": v(-247.65, 765.17) * mm, "mid": v(-250.83, 768.35) * mm, "end": v(-254, 765.17) * mm});
            skLineSegment(sketch, "E42.2.0.1", {"start": v(-254, 765.17) * mm, "end": v(-254, 758.83) * mm});
            skArc(sketch, "E42.2.0.2", {"start": v(-254, 758.83) * mm, "mid": v(-250.83, 755.65) * mm, "end": v(-247.65, 758.83) * mm});
            skLineSegment(sketch, "E42.2.0.3", {"start": v(-247.65, 758.83) * mm, "end": v(-107.95, 758.83) * mm});
            skLineSegment(sketch, "E42.2.0.4", {"start": v(-247.65, 765.17) * mm, "end": v(-107.95, 765.17) * mm});
            skArc(sketch, "E42.2.0.5", {"start": v(-101.6, 765.17) * mm, "mid": v(-104.77, 768.35) * mm, "end": v(-107.95, 765.17) * mm});
            skLineSegment(sketch, "E42.2.0.6", {"start": v(-101.6, 765.17) * mm, "end": v(-101.6, 758.83) * mm});
            skArc(sketch, "E42.2.0.7", {"start": v(-107.95, 758.83) * mm, "mid": v(-104.77, 755.65) * mm, "end": v(-101.6, 758.83) * mm});
            skArc(sketch, "E42.2.1.0", {"start": v(-247.65, 460.38) * mm, "mid": v(-250.83, 463.55) * mm, "end": v(-254, 460.38) * mm});
            skLineSegment(sketch, "E42.2.1.1", {"start": v(-254, 460.38) * mm, "end": v(-254, 454.03) * mm});
            skArc(sketch, "E42.2.1.2", {"start": v(-254, 454.03) * mm, "mid": v(-250.83, 450.85) * mm, "end": v(-247.65, 454.03) * mm});
            skLineSegment(sketch, "E42.2.1.3", {"start": v(-247.65, 454.03) * mm, "end": v(-107.95, 454.03) * mm});
            skLineSegment(sketch, "E42.2.1.4", {"start": v(-247.65, 460.38) * mm, "end": v(-107.95, 460.38) * mm});
            skArc(sketch, "E42.2.1.5", {"start": v(-101.6, 460.38) * mm, "mid": v(-104.77, 463.55) * mm, "end": v(-107.95, 460.38) * mm});
            skLineSegment(sketch, "E42.2.1.6", {"start": v(-101.6, 460.38) * mm, "end": v(-101.6, 454.03) * mm});
            skArc(sketch, "E42.2.1.7", {"start": v(-107.95, 454.03) * mm, "mid": v(-104.77, 450.85) * mm, "end": v(-101.6, 454.03) * mm});
            skArc(sketch, "E42.2.2.0", {"start": v(-247.65, 155.58) * mm, "mid": v(-250.83, 158.75) * mm, "end": v(-254, 155.58) * mm});
            skLineSegment(sketch, "E42.2.2.1", {"start": v(-254, 155.58) * mm, "end": v(-254, 149.23) * mm});
            skArc(sketch, "E42.2.2.2", {"start": v(-254, 149.23) * mm, "mid": v(-250.83, 146.05) * mm, "end": v(-247.65, 149.23) * mm});
            skLineSegment(sketch, "E42.2.2.3", {"start": v(-247.65, 149.23) * mm, "end": v(-107.95, 149.23) * mm});
            skLineSegment(sketch, "E42.2.2.4", {"start": v(-247.65, 155.58) * mm, "end": v(-107.95, 155.58) * mm});
            skArc(sketch, "E42.2.2.5", {"start": v(-101.6, 155.58) * mm, "mid": v(-104.77, 158.75) * mm, "end": v(-107.95, 155.58) * mm});
            skLineSegment(sketch, "E42.2.2.6", {"start": v(-101.6, 155.58) * mm, "end": v(-101.6, 149.23) * mm});
            skArc(sketch, "E42.2.2.7", {"start": v(-107.95, 149.23) * mm, "mid": v(-104.77, 146.05) * mm, "end": v(-101.6, 149.23) * mm});
            skArc(sketch, "E42.3.0.0", {"start": v(107.95, 765.17) * mm, "mid": v(104.77, 768.35) * mm, "end": v(101.6, 765.17) * mm});
            skLineSegment(sketch, "E42.3.0.1", {"start": v(101.6, 765.17) * mm, "end": v(101.6, 758.83) * mm});
            skArc(sketch, "E42.3.0.2", {"start": v(101.6, 758.83) * mm, "mid": v(104.77, 755.65) * mm, "end": v(107.95, 758.83) * mm});
            skLineSegment(sketch, "E42.3.0.3", {"start": v(107.95, 758.83) * mm, "end": v(247.65, 758.83) * mm});
            skLineSegment(sketch, "E42.3.0.4", {"start": v(107.95, 765.17) * mm, "end": v(247.65, 765.17) * mm});
            skArc(sketch, "E42.3.0.5", {"start": v(254, 765.17) * mm, "mid": v(250.83, 768.35) * mm, "end": v(247.65, 765.17) * mm});
            skLineSegment(sketch, "E42.3.0.6", {"start": v(254, 765.17) * mm, "end": v(254, 758.83) * mm});
            skArc(sketch, "E42.3.0.7", {"start": v(247.65, 758.83) * mm, "mid": v(250.83, 755.65) * mm, "end": v(254, 758.83) * mm});
            skArc(sketch, "E42.3.1.0", {"start": v(107.95, 460.38) * mm, "mid": v(104.77, 463.55) * mm, "end": v(101.6, 460.38) * mm});
            skLineSegment(sketch, "E42.3.1.1", {"start": v(101.6, 460.38) * mm, "end": v(101.6, 454.03) * mm});
            skArc(sketch, "E42.3.1.2", {"start": v(101.6, 454.03) * mm, "mid": v(104.77, 450.85) * mm, "end": v(107.95, 454.03) * mm});
            skLineSegment(sketch, "E42.3.1.3", {"start": v(107.95, 454.03) * mm, "end": v(247.65, 454.03) * mm});
            skLineSegment(sketch, "E42.3.1.4", {"start": v(107.95, 460.38) * mm, "end": v(247.65, 460.38) * mm});
            skArc(sketch, "E42.3.1.5", {"start": v(254, 460.38) * mm, "mid": v(250.83, 463.55) * mm, "end": v(247.65, 460.38) * mm});
            skLineSegment(sketch, "E42.3.1.6", {"start": v(254, 460.38) * mm, "end": v(254, 454.03) * mm});
            skArc(sketch, "E42.3.1.7", {"start": v(247.65, 454.03) * mm, "mid": v(250.83, 450.85) * mm, "end": v(254, 454.03) * mm});
            skArc(sketch, "E42.3.2.0", {"start": v(107.95, 155.58) * mm, "mid": v(104.77, 158.75) * mm, "end": v(101.6, 155.58) * mm});
            skLineSegment(sketch, "E42.3.2.1", {"start": v(101.6, 155.58) * mm, "end": v(101.6, 149.23) * mm});
            skArc(sketch, "E42.3.2.2", {"start": v(101.6, 149.23) * mm, "mid": v(104.77, 146.05) * mm, "end": v(107.95, 149.23) * mm});
            skLineSegment(sketch, "E42.3.2.3", {"start": v(107.95, 149.23) * mm, "end": v(247.65, 149.23) * mm});
            skLineSegment(sketch, "E42.3.2.4", {"start": v(107.95, 155.58) * mm, "end": v(247.65, 155.58) * mm});
            skArc(sketch, "E42.3.2.5", {"start": v(254, 155.58) * mm, "mid": v(250.83, 158.75) * mm, "end": v(247.65, 155.58) * mm});
            skLineSegment(sketch, "E42.3.2.6", {"start": v(254, 155.58) * mm, "end": v(254, 149.23) * mm});
            skArc(sketch, "E42.3.2.7", {"start": v(247.65, 149.23) * mm, "mid": v(250.83, 146.05) * mm, "end": v(254, 149.23) * mm});
            skArc(sketch, "E42.4.0.0", {"start": v(463.55, 765.17) * mm, "mid": v(460.37, 768.35) * mm, "end": v(457.2, 765.17) * mm});
            skLineSegment(sketch, "E42.4.0.1", {"start": v(457.2, 765.17) * mm, "end": v(457.2, 758.83) * mm});
            skArc(sketch, "E42.4.0.2", {"start": v(457.2, 758.83) * mm, "mid": v(460.37, 755.65) * mm, "end": v(463.55, 758.83) * mm});
            skLineSegment(sketch, "E42.4.0.3", {"start": v(463.55, 758.83) * mm, "end": v(603.25, 758.83) * mm});
            skLineSegment(sketch, "E42.4.0.4", {"start": v(463.55, 765.17) * mm, "end": v(603.25, 765.17) * mm});
            skArc(sketch, "E42.4.0.5", {"start": v(609.6, 765.17) * mm, "mid": v(606.43, 768.35) * mm, "end": v(603.25, 765.17) * mm});
            skLineSegment(sketch, "E42.4.0.6", {"start": v(609.6, 765.17) * mm, "end": v(609.6, 758.83) * mm});
            skArc(sketch, "E42.4.0.7", {"start": v(603.25, 758.83) * mm, "mid": v(606.43, 755.65) * mm, "end": v(609.6, 758.83) * mm});
            skArc(sketch, "E42.4.1.0", {"start": v(463.55, 460.38) * mm, "mid": v(460.37, 463.55) * mm, "end": v(457.2, 460.38) * mm});
            skLineSegment(sketch, "E42.4.1.1", {"start": v(457.2, 460.38) * mm, "end": v(457.2, 454.03) * mm});
            skArc(sketch, "E42.4.1.2", {"start": v(457.2, 454.03) * mm, "mid": v(460.37, 450.85) * mm, "end": v(463.55, 454.03) * mm});
            skLineSegment(sketch, "E42.4.1.3", {"start": v(463.55, 454.03) * mm, "end": v(603.25, 454.03) * mm});
            skLineSegment(sketch, "E42.4.1.4", {"start": v(463.55, 460.38) * mm, "end": v(603.25, 460.38) * mm});
            skArc(sketch, "E42.4.1.5", {"start": v(609.6, 460.38) * mm, "mid": v(606.43, 463.55) * mm, "end": v(603.25, 460.38) * mm});
            skLineSegment(sketch, "E42.4.1.6", {"start": v(609.6, 460.38) * mm, "end": v(609.6, 454.03) * mm});
            skArc(sketch, "E42.4.1.7", {"start": v(603.25, 454.03) * mm, "mid": v(606.43, 450.85) * mm, "end": v(609.6, 454.03) * mm});
            skArc(sketch, "E42.4.2.0", {"start": v(463.55, 155.58) * mm, "mid": v(460.37, 158.75) * mm, "end": v(457.2, 155.58) * mm});
            skLineSegment(sketch, "E42.4.2.1", {"start": v(457.2, 155.58) * mm, "end": v(457.2, 149.23) * mm});
            skArc(sketch, "E42.4.2.2", {"start": v(457.2, 149.23) * mm, "mid": v(460.37, 146.05) * mm, "end": v(463.55, 149.23) * mm});
            skLineSegment(sketch, "E42.4.2.3", {"start": v(463.55, 149.23) * mm, "end": v(603.25, 149.23) * mm});
            skLineSegment(sketch, "E42.4.2.4", {"start": v(463.55, 155.58) * mm, "end": v(603.25, 155.58) * mm});
            skArc(sketch, "E42.4.2.5", {"start": v(609.6, 155.58) * mm, "mid": v(606.43, 158.75) * mm, "end": v(603.25, 155.58) * mm});
            skLineSegment(sketch, "E42.4.2.6", {"start": v(609.6, 155.58) * mm, "end": v(609.6, 149.23) * mm});
            skArc(sketch, "E42.4.2.7", {"start": v(603.25, 149.23) * mm, "mid": v(606.43, 146.05) * mm, "end": v(609.6, 149.23) * mm});
            skArc(sketch, "E42.5.0.0", {"start": v(819.15, 765.17) * mm, "mid": v(815.97, 768.35) * mm, "end": v(812.8, 765.17) * mm});
            skLineSegment(sketch, "E42.5.0.1", {"start": v(812.8, 765.17) * mm, "end": v(812.8, 758.83) * mm});
            skArc(sketch, "E42.5.0.2", {"start": v(812.8, 758.83) * mm, "mid": v(815.97, 755.65) * mm, "end": v(819.15, 758.83) * mm});
            skLineSegment(sketch, "E42.5.0.3", {"start": v(819.15, 758.83) * mm, "end": v(958.85, 758.83) * mm});
            skLineSegment(sketch, "E42.5.0.4", {"start": v(819.15, 765.17) * mm, "end": v(958.85, 765.17) * mm});
            skArc(sketch, "E42.5.0.5", {"start": v(965.2, 765.17) * mm, "mid": v(962.03, 768.35) * mm, "end": v(958.85, 765.17) * mm});
            skLineSegment(sketch, "E42.5.0.6", {"start": v(965.2, 765.17) * mm, "end": v(965.2, 758.83) * mm});
            skArc(sketch, "E42.5.0.7", {"start": v(958.85, 758.83) * mm, "mid": v(962.03, 755.65) * mm, "end": v(965.2, 758.83) * mm});
            skArc(sketch, "E42.5.1.0", {"start": v(819.15, 460.38) * mm, "mid": v(815.97, 463.55) * mm, "end": v(812.8, 460.38) * mm});
            skLineSegment(sketch, "E42.5.1.1", {"start": v(812.8, 460.38) * mm, "end": v(812.8, 454.03) * mm});
            skArc(sketch, "E42.5.1.2", {"start": v(812.8, 454.03) * mm, "mid": v(815.97, 450.85) * mm, "end": v(819.15, 454.03) * mm});
            skLineSegment(sketch, "E42.5.1.3", {"start": v(819.15, 454.03) * mm, "end": v(958.85, 454.03) * mm});
            skLineSegment(sketch, "E42.5.1.4", {"start": v(819.15, 460.38) * mm, "end": v(958.85, 460.38) * mm});
            skArc(sketch, "E42.5.1.5", {"start": v(965.2, 460.38) * mm, "mid": v(962.03, 463.55) * mm, "end": v(958.85, 460.38) * mm});
            skLineSegment(sketch, "E42.5.1.6", {"start": v(965.2, 460.38) * mm, "end": v(965.2, 454.03) * mm});
            skArc(sketch, "E42.5.1.7", {"start": v(958.85, 454.03) * mm, "mid": v(962.03, 450.85) * mm, "end": v(965.2, 454.03) * mm});
            skArc(sketch, "E42.5.2.0", {"start": v(819.15, 155.58) * mm, "mid": v(815.97, 158.75) * mm, "end": v(812.8, 155.58) * mm});
            skLineSegment(sketch, "E42.5.2.1", {"start": v(812.8, 155.58) * mm, "end": v(812.8, 149.23) * mm});
            skArc(sketch, "E42.5.2.2", {"start": v(812.8, 149.23) * mm, "mid": v(815.97, 146.05) * mm, "end": v(819.15, 149.23) * mm});
            skLineSegment(sketch, "E42.5.2.3", {"start": v(819.15, 149.23) * mm, "end": v(958.85, 149.23) * mm});
            skLineSegment(sketch, "E42.5.2.4", {"start": v(819.15, 155.58) * mm, "end": v(958.85, 155.58) * mm});
            skArc(sketch, "E42.5.2.5", {"start": v(965.2, 155.58) * mm, "mid": v(962.03, 158.75) * mm, "end": v(958.85, 155.58) * mm});
            skLineSegment(sketch, "E42.5.2.6", {"start": v(965.2, 155.58) * mm, "end": v(965.2, 149.23) * mm});
            skArc(sketch, "E42.5.2.7", {"start": v(958.85, 149.23) * mm, "mid": v(962.03, 146.05) * mm, "end": v(965.2, 149.23) * mm});
            skLineSegment(sketch, "E42.direction1", {"start": v(-965.2, 758.83) * mm, "end": v(-609.6, 758.83) * mm, "construction": true});
            skLineSegment(sketch, "E42.direction2", {"start": v(-965.2, 758.83) * mm, "end": v(-965.2, 454.03) * mm, "construction": true});
            skSolve(sketch);
        }
        {
            var Q0;
            Q0 = qSketchRegion(id + "F4", true);
            extrude(context, id + "F5", {"entities" : qUnion([Q0]), "operationType" : NewBodyOperationType.REMOVE, "endBound" : BoundingType.THROUGH_ALL, "oppositeDirection" : true, "depth" : 25.4 * mm});
        }
        {
            var Q0;
            Q0=makeQuery(id+"F1.opExtrude","CAP_FACE",FACE,{"disambiguationData":[OSD([sQuery(id+"F0.wireOp",EDGE,"E0.bottom"),sQuery(id+"F0.wireOp",EDGE,"E0.top"),sQuery(id+"F0.wireOp",EDGE,"E0.left"),sQuery(id+"F0.wireOp",EDGE,"E0.right"),sQuery(id+"F0.wireOp",EDGE,"E1.filletArc"),sQuery(id+"F0.wireOp",EDGE,"E2.filletArc"),sQuery(id+"F0.wireOp",EDGE,"E3.filletArc"),sQuery(id+"F0.wireOp",EDGE,"E4.filletArc")])],"isStart":false});
            var sketch = newSketch(context, id + "F6", { "sketchPlane" : qUnion([Q0])});
            skLineSegment(sketch, "E43.bottom", {"start": v(-787.4, 0) * mm, "end": v(-736.6, 0) * mm});
            skLineSegment(sketch, "E43.left", {"start": v(-787.4, 0) * mm, "end": v(-787.4, 6.35) * mm});
            skLineSegment(sketch, "E43.right", {"start": v(-736.6, 0) * mm, "end": v(-736.6, 6.35) * mm});
            skLineSegment(sketch, "E44.top", {"start": v(-685.8, 0) * mm, "end": v(-635, 0) * mm});
            skLineSegment(sketch, "E44.left", {"start": v(-685.8, 6.35) * mm, "end": v(-685.8, 0) * mm});
            skLineSegment(sketch, "E44.right", {"start": v(-635, 6.35) * mm, "end": v(-635, 0) * mm});
            skArc(sketch, "E45", {"start": v(-781.05, 6.35) * mm, "mid": v(-784.23, 9.52) * mm, "end": v(-787.4, 6.35) * mm});
            skArc(sketch, "E46", {"start": v(-635, 6.35) * mm, "mid": v(-638.18, 9.52) * mm, "end": v(-641.35, 6.35) * mm});
            skLineSegment(sketch, "E47.trimOffspring", {"start": v(-781.05, 6.35) * mm, "end": v(-742.95, 6.35) * mm});
            skArc(sketch, "E48", {"start": v(-736.6, 6.35) * mm, "mid": v(-739.78, 9.52) * mm, "end": v(-742.95, 6.35) * mm});
            skArc(sketch, "E49", {"start": v(-679.45, 6.35) * mm, "mid": v(-682.63, 9.52) * mm, "end": v(-685.8, 6.35) * mm});
            skLineSegment(sketch, "E50.trimOffspring", {"start": v(-679.45, 6.35) * mm, "end": v(-641.35, 6.35) * mm});
            skLineSegment(sketch, "E51.1.0.0", {"start": v(-431.8, 0) * mm, "end": v(-381, 0) * mm});
            skLineSegment(sketch, "E51.1.0.1", {"start": v(-431.8, 0) * mm, "end": v(-431.8, 6.35) * mm});
            skArc(sketch, "E51.1.0.2", {"start": v(-425.45, 6.35) * mm, "mid": v(-428.63, 9.52) * mm, "end": v(-431.8, 6.35) * mm});
            skLineSegment(sketch, "E51.1.0.3", {"start": v(-425.45, 6.35) * mm, "end": v(-387.35, 6.35) * mm});
            skArc(sketch, "E51.1.0.4", {"start": v(-381, 6.35) * mm, "mid": v(-384.18, 9.52) * mm, "end": v(-387.35, 6.35) * mm});
            skLineSegment(sketch, "E51.1.0.5", {"start": v(-381, 0) * mm, "end": v(-381, 6.35) * mm});
            skLineSegment(sketch, "E51.1.0.6", {"start": v(-330.2, 6.35) * mm, "end": v(-330.2, 0) * mm});
            skLineSegment(sketch, "E51.1.0.7", {"start": v(-330.2, 0) * mm, "end": v(-279.4, 0) * mm});
            skLineSegment(sketch, "E51.1.0.8", {"start": v(-279.4, 6.35) * mm, "end": v(-279.4, 0) * mm});
            skArc(sketch, "E51.1.0.9", {"start": v(-279.4, 6.35) * mm, "mid": v(-282.57, 9.52) * mm, "end": v(-285.75, 6.35) * mm});
            skLineSegment(sketch, "E51.1.0.10", {"start": v(-323.85, 6.35) * mm, "end": v(-285.75, 6.35) * mm});
            skArc(sketch, "E51.1.0.11", {"start": v(-323.85, 6.35) * mm, "mid": v(-327.03, 9.52) * mm, "end": v(-330.2, 6.35) * mm});
            skLineSegment(sketch, "E51.2.0.0", {"start": v(-76.2, 0) * mm, "end": v(-25.4, 0) * mm});
            skLineSegment(sketch, "E51.2.0.1", {"start": v(-76.2, 0) * mm, "end": v(-76.2, 6.35) * mm});
            skArc(sketch, "E51.2.0.2", {"start": v(-69.85, 6.35) * mm, "mid": v(-73.02, 9.52) * mm, "end": v(-76.2, 6.35) * mm});
            skLineSegment(sketch, "E51.2.0.3", {"start": v(-69.85, 6.35) * mm, "end": v(-31.75, 6.35) * mm});
            skArc(sketch, "E51.2.0.4", {"start": v(-25.4, 6.35) * mm, "mid": v(-28.57, 9.52) * mm, "end": v(-31.75, 6.35) * mm});
            skLineSegment(sketch, "E51.2.0.5", {"start": v(-25.4, 0) * mm, "end": v(-25.4, 6.35) * mm});
            skLineSegment(sketch, "E51.2.0.6", {"start": v(25.4, 6.35) * mm, "end": v(25.4, 0) * mm});
            skLineSegment(sketch, "E51.2.0.7", {"start": v(25.4, 0) * mm, "end": v(76.2, 0) * mm});
            skLineSegment(sketch, "E51.2.0.8", {"start": v(76.2, 6.35) * mm, "end": v(76.2, 0) * mm});
            skArc(sketch, "E51.2.0.9", {"start": v(76.2, 6.35) * mm, "mid": v(73.03, 9.52) * mm, "end": v(69.85, 6.35) * mm});
            skLineSegment(sketch, "E51.2.0.10", {"start": v(31.75, 6.35) * mm, "end": v(69.85, 6.35) * mm});
            skArc(sketch, "E51.2.0.11", {"start": v(31.75, 6.35) * mm, "mid": v(28.57, 9.52) * mm, "end": v(25.4, 6.35) * mm});
            skLineSegment(sketch, "E51.3.0.0", {"start": v(279.4, 0) * mm, "end": v(330.2, 0) * mm});
            skLineSegment(sketch, "E51.3.0.1", {"start": v(279.4, 0) * mm, "end": v(279.4, 6.35) * mm});
            skArc(sketch, "E51.3.0.2", {"start": v(285.75, 6.35) * mm, "mid": v(282.58, 9.52) * mm, "end": v(279.4, 6.35) * mm});
            skLineSegment(sketch, "E51.3.0.3", {"start": v(285.75, 6.35) * mm, "end": v(323.85, 6.35) * mm});
            skArc(sketch, "E51.3.0.4", {"start": v(330.2, 6.35) * mm, "mid": v(327.03, 9.52) * mm, "end": v(323.85, 6.35) * mm});
            skLineSegment(sketch, "E51.3.0.5", {"start": v(330.2, 0) * mm, "end": v(330.2, 6.35) * mm});
            skLineSegment(sketch, "E51.3.0.6", {"start": v(381, 6.35) * mm, "end": v(381, 0) * mm});
            skLineSegment(sketch, "E51.3.0.7", {"start": v(381, 0) * mm, "end": v(431.8, 0) * mm});
            skLineSegment(sketch, "E51.3.0.8", {"start": v(431.8, 6.35) * mm, "end": v(431.8, 0) * mm});
            skArc(sketch, "E51.3.0.9", {"start": v(431.8, 6.35) * mm, "mid": v(428.63, 9.52) * mm, "end": v(425.45, 6.35) * mm});
            skLineSegment(sketch, "E51.3.0.10", {"start": v(387.35, 6.35) * mm, "end": v(425.45, 6.35) * mm});
            skArc(sketch, "E51.3.0.11", {"start": v(387.35, 6.35) * mm, "mid": v(384.17, 9.52) * mm, "end": v(381, 6.35) * mm});
            skLineSegment(sketch, "E51.4.0.0", {"start": v(635, 0) * mm, "end": v(685.8, 0) * mm});
            skLineSegment(sketch, "E51.4.0.1", {"start": v(635, 0) * mm, "end": v(635, 6.35) * mm});
            skArc(sketch, "E51.4.0.2", {"start": v(641.35, 6.35) * mm, "mid": v(638.18, 9.52) * mm, "end": v(635, 6.35) * mm});
            skLineSegment(sketch, "E51.4.0.3", {"start": v(641.35, 6.35) * mm, "end": v(679.45, 6.35) * mm});
            skArc(sketch, "E51.4.0.4", {"start": v(685.8, 6.35) * mm, "mid": v(682.63, 9.52) * mm, "end": v(679.45, 6.35) * mm});
            skLineSegment(sketch, "E51.4.0.5", {"start": v(685.8, 0) * mm, "end": v(685.8, 6.35) * mm});
            skLineSegment(sketch, "E51.4.0.6", {"start": v(736.6, 6.35) * mm, "end": v(736.6, 0) * mm});
            skLineSegment(sketch, "E51.4.0.7", {"start": v(736.6, 0) * mm, "end": v(787.4, 0) * mm});
            skLineSegment(sketch, "E51.4.0.8", {"start": v(787.4, 6.35) * mm, "end": v(787.4, 0) * mm});
            skArc(sketch, "E51.4.0.9", {"start": v(787.4, 6.35) * mm, "mid": v(784.23, 9.52) * mm, "end": v(781.05, 6.35) * mm});
            skLineSegment(sketch, "E51.4.0.10", {"start": v(742.95, 6.35) * mm, "end": v(781.05, 6.35) * mm});
            skArc(sketch, "E51.4.0.11", {"start": v(742.95, 6.35) * mm, "mid": v(739.77, 9.52) * mm, "end": v(736.6, 6.35) * mm});
            skLineSegment(sketch, "E51.direction1", {"start": v(-787.4, 0) * mm, "end": v(-431.8, 0) * mm, "construction": true});
            skSolve(sketch);
        }
        {
            var Q0;
            Q0 = qSketchRegion(id + "F6", true);
            extrude(context, id + "F7", {"entities" : qUnion([Q0]), "operationType" : NewBodyOperationType.REMOVE, "endBound" : BoundingType.THROUGH_ALL, "oppositeDirection" : true, "depth" : 25.4 * mm});
        }
        {
            var Q0;
            Q0=makeQuery(id+"F2.imprint","IMPRINT",FACE,{"disambiguationData":[TD([[makeQuery(id+"F2.imprint","IMPRINT",EDGE,{"derivedFrom":sQuery(id+"F2.wireOp",EDGE,"E22")}),-1.0]])]});
            var sketch = newSketch(context, id + "F8", { "sketchPlane" : qUnion([Q0])});
            skLineSegment(sketch, "E52.bottom", {"start": v(-812.8, 812.8) * mm, "end": v(812.8, 812.8) * mm, "construction": true});
            skLineSegment(sketch, "E52.top", {"start": v(-812.8, 101.6) * mm, "end": v(812.8, 101.6) * mm, "construction": true});
            skLineSegment(sketch, "E52.left", {"start": v(-812.8, 812.8) * mm, "end": v(-812.8, 101.6) * mm, "construction": true});
            skLineSegment(sketch, "E52.right", {"start": v(812.8, 812.8) * mm, "end": v(812.8, 101.6) * mm, "construction": true});
            skLineSegment(sketch, "E53", {"start": v(-812.8, 647.7) * mm, "end": v(-647.7, 812.8) * mm, "construction": true});
            skLineSegment(sketch, "E54", {"start": v(647.7, 812.8) * mm, "end": v(812.8, 647.7) * mm, "construction": true});
            skLineSegment(sketch, "E55", {"start": v(812.8, 266.7) * mm, "end": v(647.7, 101.6) * mm, "construction": true});
            skLineSegment(sketch, "E56", {"start": v(-812.8, 266.7) * mm, "end": v(-647.7, 101.6) * mm, "construction": true});
            skCircle(sketch, "E57", {"center": v(-647.7, 812.8) * mm, "radius": 3.3 * mm});
            skCircle(sketch, "E58", {"center": v(-812.8, 647.7) * mm, "radius": 3.3 * mm});
            skCircle(sketch, "E59", {"center": v(-812.8, 266.7) * mm, "radius": 3.3 * mm});
            skCircle(sketch, "E60", {"center": v(-647.7, 101.6) * mm, "radius": 3.3 * mm});
            skCircle(sketch, "E61", {"center": v(647.7, 101.6) * mm, "radius": 3.3 * mm});
            skCircle(sketch, "E62", {"center": v(812.8, 266.7) * mm, "radius": 3.3 * mm});
            skCircle(sketch, "E63", {"center": v(812.8, 647.7) * mm, "radius": 3.3 * mm});
            skCircle(sketch, "E64", {"center": v(647.7, 812.8) * mm, "radius": 3.3 * mm});
            skLineSegment(sketch, "E65", {"start": v(-647.7, 812.8) * mm, "end": v(-215.9, 812.8) * mm, "construction": true});
            skLineSegment(sketch, "E66", {"start": v(-215.9, 812.8) * mm, "end": v(215.9, 812.8) * mm, "construction": true});
            skLineSegment(sketch, "E67", {"start": v(215.9, 812.8) * mm, "end": v(647.7, 812.8) * mm, "construction": true});
            skCircle(sketch, "E68", {"center": v(-215.9, 812.8) * mm, "radius": 3.3 * mm});
            skCircle(sketch, "E69", {"center": v(215.9, 812.8) * mm, "radius": 3.3 * mm});
            skCircle(sketch, "E70", {"center": v(-215.9, 101.6) * mm, "radius": 3.3 * mm});
            skCircle(sketch, "E71", {"center": v(215.9, 101.6) * mm, "radius": 3.3 * mm});
            skSolve(sketch);
        }
        {
            var Q0;
            Q0 = qSketchRegion(id + "F8", true);
            extrude(context, id + "F9", {"entities" : qUnion([Q0]), "operationType" : NewBodyOperationType.REMOVE, "endBound" : BoundingType.THROUGH_ALL, "oppositeDirection" : true, "depth" : 25.4 * mm});
        }
        {
            var Q0;
            Q0=makeQuery(id+"F1.opExtrude","CAP_FACE",FACE,{"disambiguationData":[OSD([sQuery(id+"F0.wireOp",EDGE,"E0.bottom"),sQuery(id+"F0.wireOp",EDGE,"E0.top"),sQuery(id+"F0.wireOp",EDGE,"E0.left"),sQuery(id+"F0.wireOp",EDGE,"E0.right"),sQuery(id+"F0.wireOp",EDGE,"E1.filletArc"),sQuery(id+"F0.wireOp",EDGE,"E2.filletArc"),sQuery(id+"F0.wireOp",EDGE,"E3.filletArc"),sQuery(id+"F0.wireOp",EDGE,"E4.filletArc")])],"isStart":false});
            var sketch = newSketch(context, id + "F10", { "sketchPlane" : qUnion([Q0])});
            skLineSegment(sketch, "E72.bottom", {"start": v(-161.92, 863.6) * mm, "end": v(-41.27, 863.6) * mm});
            skLineSegment(sketch, "E72.top", {"start": v(-161.92, 820.42) * mm, "end": v(-41.27, 820.42) * mm});
            skLineSegment(sketch, "E72.left", {"start": v(-165.1, 860.43) * mm, "end": v(-165.1, 823.6) * mm});
            skLineSegment(sketch, "E72.right", {"start": v(-38.1, 860.43) * mm, "end": v(-38.1, 823.6) * mm});
            skPoint(sketch, "E73.visualSharp", {"position": v(-165.1, 863.6) * mm});
            skArc(sketch, "E73.filletArc", {"start": v(-161.92, 863.6) * mm, "mid": v(-164.17, 862.67) * mm, "end": v(-165.1, 860.43) * mm});
            skPoint(sketch, "E74.visualSharp", {"position": v(-165.1, 820.42) * mm});
            skArc(sketch, "E74.filletArc", {"start": v(-165.1, 823.6) * mm, "mid": v(-164.17, 821.35) * mm, "end": v(-161.92, 820.42) * mm});
            skPoint(sketch, "E75.visualSharp", {"position": v(-38.1, 863.6) * mm});
            skArc(sketch, "E75.filletArc", {"start": v(-38.1, 860.43) * mm, "mid": v(-39.03, 862.67) * mm, "end": v(-41.27, 863.6) * mm});
            skPoint(sketch, "E76.visualSharp", {"position": v(-38.1, 820.42) * mm});
            skArc(sketch, "E76.filletArc", {"start": v(-41.27, 820.42) * mm, "mid": v(-39.03, 821.35) * mm, "end": v(-38.1, 823.6) * mm});
            skArc(sketch, "E77.MirrorCS", {"start": v(41.27, 820.42) * mm, "mid": v(39.03, 821.35) * mm, "end": v(38.1, 823.6) * mm});
            skArc(sketch, "E78.MirrorCS", {"start": v(38.1, 860.43) * mm, "mid": v(39.03, 862.67) * mm, "end": v(41.27, 863.6) * mm});
            skArc(sketch, "E79.MirrorCS", {"start": v(165.1, 823.6) * mm, "mid": v(164.17, 821.35) * mm, "end": v(161.92, 820.42) * mm});
            skArc(sketch, "E80.MirrorCS", {"start": v(161.92, 863.6) * mm, "mid": v(164.17, 862.67) * mm, "end": v(165.1, 860.43) * mm});
            skPoint(sketch, "E81.MirrorP", {"position": v(38.1, 820.42) * mm});
            skPoint(sketch, "E82.MirrorP", {"position": v(38.1, 863.6) * mm});
            skPoint(sketch, "E83.MirrorP", {"position": v(165.1, 820.42) * mm});
            skPoint(sketch, "E84.MirrorP", {"position": v(165.1, 863.6) * mm});
            skLineSegment(sketch, "E85.MirrorCS", {"start": v(38.1, 860.43) * mm, "end": v(38.1, 823.6) * mm});
            skLineSegment(sketch, "E86.MirrorCS", {"start": v(165.1, 860.43) * mm, "end": v(165.1, 823.6) * mm});
            skLineSegment(sketch, "E87.MirrorCS", {"start": v(161.92, 863.6) * mm, "end": v(41.27, 863.6) * mm});
            skLineSegment(sketch, "E88.MirrorCS", {"start": v(161.92, 820.42) * mm, "end": v(41.27, 820.42) * mm});
            skSolve(sketch);
        }
        {
            var Q0;
            Q0 = qSketchRegion(id + "F10", true);
            extrude(context, id + "F11", {"entities" : qUnion([Q0]), "operationType" : NewBodyOperationType.REMOVE, "endBound" : BoundingType.THROUGH_ALL, "oppositeDirection" : true, "depth" : 25.4 * mm});
        }
        {
            var Q0;
            Q0=makeQuery(id+"F1.opExtrude","CAP_FACE",FACE,{"disambiguationData":[OSD([sQuery(id+"F0.wireOp",EDGE,"E0.bottom"),sQuery(id+"F0.wireOp",EDGE,"E0.top"),sQuery(id+"F0.wireOp",EDGE,"E0.left"),sQuery(id+"F0.wireOp",EDGE,"E0.right"),sQuery(id+"F0.wireOp",EDGE,"E1.filletArc"),sQuery(id+"F0.wireOp",EDGE,"E2.filletArc"),sQuery(id+"F0.wireOp",EDGE,"E3.filletArc"),sQuery(id+"F0.wireOp",EDGE,"E4.filletArc")])],"isStart":false});
            var sketch = newSketch(context, id + "F12", { "sketchPlane" : qUnion([Q0])});
            skLineSegment(sketch, "E89", {"start": v(-600.07, 876.3) * mm, "end": v(-447.67, 876.3) * mm});
            skLineSegment(sketch, "E90", {"start": v(-600.07, 825.5) * mm, "end": v(-447.67, 825.5) * mm});
            skArc(sketch, "E91", {"start": v(-600.07, 876.3) * mm, "mid": v(-625.47, 850.9) * mm, "end": v(-600.07, 825.5) * mm});
            skArc(sketch, "E92", {"start": v(-447.67, 825.5) * mm, "mid": v(-422.27, 850.9) * mm, "end": v(-447.67, 876.3) * mm});
            skLineSegment(sketch, "E93.MirrorCS", {"start": v(600.07, 825.5) * mm, "end": v(447.67, 825.5) * mm});
            skLineSegment(sketch, "E94.MirrorCS", {"start": v(600.07, 876.3) * mm, "end": v(447.67, 876.3) * mm});
            skArc(sketch, "E95.MirrorCS", {"start": v(447.67, 825.5) * mm, "mid": v(422.27, 850.9) * mm, "end": v(447.67, 876.3) * mm});
            skArc(sketch, "E96.MirrorCS", {"start": v(600.07, 876.3) * mm, "mid": v(625.47, 850.9) * mm, "end": v(600.07, 825.5) * mm});
            skSolve(sketch);
        }
        {
            var Q0;
            Q0 = qSketchRegion(id + "F12", true);
            extrude(context, id + "F13", {"entities" : qUnion([Q0]), "operationType" : NewBodyOperationType.REMOVE, "endBound" : BoundingType.THROUGH_ALL, "oppositeDirection" : true, "depth" : 25.4 * mm});
        }
        {
            var Q0;
            Q0=makeQuery(id+"F1.opExtrude","CAP_FACE",FACE,{"disambiguationData":[OSD([sQuery(id+"F0.wireOp",EDGE,"E0.bottom"),sQuery(id+"F0.wireOp",EDGE,"E0.top"),sQuery(id+"F0.wireOp",EDGE,"E0.left"),sQuery(id+"F0.wireOp",EDGE,"E0.right"),sQuery(id+"F0.wireOp",EDGE,"E1.filletArc"),sQuery(id+"F0.wireOp",EDGE,"E2.filletArc"),sQuery(id+"F0.wireOp",EDGE,"E3.filletArc"),sQuery(id+"F0.wireOp",EDGE,"E4.filletArc")])],"isStart":false});
            var sketch = newSketch(context, id + "F14", { "sketchPlane" : qUnion([Q0])});
            skCircle(sketch, "E97", {"center": v(38.1, 685.8) * mm, "radius": 1.63 * mm});
            skCircle(sketch, "E98", {"center": v(187.96, 685.8) * mm, "radius": 1.63 * mm});
            skCircle(sketch, "E99", {"center": v(187.96, 594.36) * mm, "radius": 1.63 * mm});
            skCircle(sketch, "E100", {"center": v(38.1, 594.36) * mm, "radius": 1.63 * mm});
            skSolve(sketch);
        }
        {
            var Q0;
            Q0 = qSketchRegion(id + "F14", true);
            extrude(context, id + "F15", {"entities" : qUnion([Q0]), "operationType" : NewBodyOperationType.REMOVE, "endBound" : BoundingType.THROUGH_ALL, "oppositeDirection" : true, "depth" : 25.4 * mm});
        }
        {
            var Q0;
            Q0=makeQuery(id+"F1.opExtrude","CAP_FACE",FACE,{"disambiguationData":[OSD([sQuery(id+"F0.wireOp",EDGE,"E0.bottom"),sQuery(id+"F0.wireOp",EDGE,"E0.top"),sQuery(id+"F0.wireOp",EDGE,"E0.left"),sQuery(id+"F0.wireOp",EDGE,"E0.right"),sQuery(id+"F0.wireOp",EDGE,"E1.filletArc"),sQuery(id+"F0.wireOp",EDGE,"E2.filletArc"),sQuery(id+"F0.wireOp",EDGE,"E3.filletArc"),sQuery(id+"F0.wireOp",EDGE,"E4.filletArc")])],"isStart":false});
            var sketch = newSketch(context, id + "F16", { "sketchPlane" : qUnion([Q0])});
            skCircle(sketch, "E101", {"center": v(-698.5, 152.4) * mm, "radius": 17.22 * mm, "construction": true});
            skLineSegment(sketch, "E102", {"start": v(-707.11, 167.31) * mm, "end": v(-689.89, 167.31) * mm, "construction": true});
            skLineSegment(sketch, "E103", {"start": v(-689.89, 167.31) * mm, "end": v(-707.11, 137.49) * mm, "construction": true});
            skLineSegment(sketch, "E104", {"start": v(-707.11, 137.49) * mm, "end": v(-689.89, 137.49) * mm, "construction": true});
            skLineSegment(sketch, "E105", {"start": v(-689.89, 137.49) * mm, "end": v(-707.11, 167.31) * mm, "construction": true});
            skCircle(sketch, "E106", {"center": v(-707.11, 167.31) * mm, "radius": 3.18 * mm});
            skCircle(sketch, "E107", {"center": v(-689.89, 167.31) * mm, "radius": 3.18 * mm});
            skCircle(sketch, "E108", {"center": v(-707.11, 137.49) * mm, "radius": 3.18 * mm});
            skCircle(sketch, "E109", {"center": v(-689.89, 137.49) * mm, "radius": 3.18 * mm});
            skCircle(sketch, "E110.0.1.0", {"center": v(-707.11, 446.71) * mm, "radius": 3.18 * mm});
            skCircle(sketch, "E110.0.1.1", {"center": v(-707.11, 416.89) * mm, "radius": 3.18 * mm});
            skCircle(sketch, "E110.0.1.2", {"center": v(-689.89, 416.89) * mm, "radius": 3.18 * mm});
            skCircle(sketch, "E110.0.1.3", {"center": v(-689.89, 446.71) * mm, "radius": 3.18 * mm});
            skCircle(sketch, "E110.0.2.0", {"center": v(-707.11, 726.11) * mm, "radius": 3.18 * mm});
            skCircle(sketch, "E110.0.2.1", {"center": v(-707.11, 696.29) * mm, "radius": 3.18 * mm});
            skCircle(sketch, "E110.0.2.2", {"center": v(-689.89, 696.29) * mm, "radius": 3.18 * mm});
            skCircle(sketch, "E110.0.2.3", {"center": v(-689.89, 726.11) * mm, "radius": 3.18 * mm});
            skCircle(sketch, "E110.1.0.0", {"center": v(-427.71, 167.31) * mm, "radius": 3.18 * mm});
            skCircle(sketch, "E110.1.0.1", {"center": v(-427.71, 137.49) * mm, "radius": 3.18 * mm});
            skCircle(sketch, "E110.1.0.2", {"center": v(-410.49, 137.49) * mm, "radius": 3.18 * mm});
            skCircle(sketch, "E110.1.0.3", {"center": v(-410.49, 167.31) * mm, "radius": 3.18 * mm});
            skCircle(sketch, "E110.1.1.0", {"center": v(-427.71, 446.71) * mm, "radius": 3.18 * mm});
            skCircle(sketch, "E110.1.1.1", {"center": v(-427.71, 416.89) * mm, "radius": 3.18 * mm});
            skCircle(sketch, "E110.1.1.2", {"center": v(-410.49, 416.89) * mm, "radius": 3.18 * mm});
            skCircle(sketch, "E110.1.1.3", {"center": v(-410.49, 446.71) * mm, "radius": 3.18 * mm});
            skCircle(sketch, "E110.1.2.0", {"center": v(-427.71, 726.11) * mm, "radius": 3.18 * mm});
            skCircle(sketch, "E110.1.2.1", {"center": v(-427.71, 696.29) * mm, "radius": 3.18 * mm});
            skCircle(sketch, "E110.1.2.2", {"center": v(-410.49, 696.29) * mm, "radius": 3.18 * mm});
            skCircle(sketch, "E110.1.2.3", {"center": v(-410.49, 726.11) * mm, "radius": 3.18 * mm});
            skCircle(sketch, "E110.2.0.0", {"center": v(-148.31, 167.31) * mm, "radius": 3.18 * mm});
            skCircle(sketch, "E110.2.0.1", {"center": v(-148.31, 137.49) * mm, "radius": 3.18 * mm});
            skCircle(sketch, "E110.2.0.2", {"center": v(-131.09, 137.49) * mm, "radius": 3.18 * mm});
            skCircle(sketch, "E110.2.0.3", {"center": v(-131.09, 167.31) * mm, "radius": 3.18 * mm});
            skCircle(sketch, "E110.2.1.0", {"center": v(-148.31, 446.71) * mm, "radius": 3.18 * mm});
            skCircle(sketch, "E110.2.1.1", {"center": v(-148.31, 416.89) * mm, "radius": 3.18 * mm});
            skCircle(sketch, "E110.2.1.2", {"center": v(-131.09, 416.89) * mm, "radius": 3.18 * mm});
            skCircle(sketch, "E110.2.1.3", {"center": v(-131.09, 446.71) * mm, "radius": 3.18 * mm});
            skCircle(sketch, "E110.2.2.0", {"center": v(-148.31, 726.11) * mm, "radius": 3.18 * mm});
            skCircle(sketch, "E110.2.2.1", {"center": v(-148.31, 696.29) * mm, "radius": 3.18 * mm});
            skCircle(sketch, "E110.2.2.2", {"center": v(-131.09, 696.29) * mm, "radius": 3.18 * mm});
            skCircle(sketch, "E110.2.2.3", {"center": v(-131.09, 726.11) * mm, "radius": 3.18 * mm});
            skCircle(sketch, "E110.3.0.0", {"center": v(131.09, 167.31) * mm, "radius": 3.18 * mm});
            skCircle(sketch, "E110.3.0.1", {"center": v(131.09, 137.49) * mm, "radius": 3.18 * mm});
            skCircle(sketch, "E110.3.0.2", {"center": v(148.31, 137.49) * mm, "radius": 3.18 * mm});
            skCircle(sketch, "E110.3.0.3", {"center": v(148.31, 167.31) * mm, "radius": 3.18 * mm});
            skCircle(sketch, "E110.3.1.0", {"center": v(131.09, 446.71) * mm, "radius": 3.18 * mm});
            skCircle(sketch, "E110.3.1.1", {"center": v(131.09, 416.89) * mm, "radius": 3.18 * mm});
            skCircle(sketch, "E110.3.1.2", {"center": v(148.31, 416.89) * mm, "radius": 3.18 * mm});
            skCircle(sketch, "E110.3.1.3", {"center": v(148.31, 446.71) * mm, "radius": 3.18 * mm});
            skCircle(sketch, "E110.3.2.0", {"center": v(131.09, 726.11) * mm, "radius": 3.18 * mm});
            skCircle(sketch, "E110.3.2.1", {"center": v(131.09, 696.29) * mm, "radius": 3.18 * mm});
            skCircle(sketch, "E110.3.2.2", {"center": v(148.31, 696.29) * mm, "radius": 3.18 * mm});
            skCircle(sketch, "E110.3.2.3", {"center": v(148.31, 726.11) * mm, "radius": 3.18 * mm});
            skCircle(sketch, "E110.4.0.0", {"center": v(410.49, 167.31) * mm, "radius": 3.18 * mm});
            skCircle(sketch, "E110.4.0.1", {"center": v(410.49, 137.49) * mm, "radius": 3.18 * mm});
            skCircle(sketch, "E110.4.0.2", {"center": v(427.71, 137.49) * mm, "radius": 3.18 * mm});
            skCircle(sketch, "E110.4.0.3", {"center": v(427.71, 167.31) * mm, "radius": 3.18 * mm});
            skCircle(sketch, "E110.4.1.0", {"center": v(410.49, 446.71) * mm, "radius": 3.18 * mm});
            skCircle(sketch, "E110.4.1.1", {"center": v(410.49, 416.89) * mm, "radius": 3.18 * mm});
            skCircle(sketch, "E110.4.1.2", {"center": v(427.71, 416.89) * mm, "radius": 3.18 * mm});
            skCircle(sketch, "E110.4.1.3", {"center": v(427.71, 446.71) * mm, "radius": 3.18 * mm});
            skCircle(sketch, "E110.4.2.0", {"center": v(410.49, 726.11) * mm, "radius": 3.18 * mm});
            skCircle(sketch, "E110.4.2.1", {"center": v(410.49, 696.29) * mm, "radius": 3.18 * mm});
            skCircle(sketch, "E110.4.2.2", {"center": v(427.71, 696.29) * mm, "radius": 3.18 * mm});
            skCircle(sketch, "E110.4.2.3", {"center": v(427.71, 726.11) * mm, "radius": 3.18 * mm});
            skCircle(sketch, "E110.5.0.0", {"center": v(689.89, 167.31) * mm, "radius": 3.18 * mm});
            skCircle(sketch, "E110.5.0.1", {"center": v(689.89, 137.49) * mm, "radius": 3.18 * mm});
            skCircle(sketch, "E110.5.0.2", {"center": v(707.11, 137.49) * mm, "radius": 3.18 * mm});
            skCircle(sketch, "E110.5.0.3", {"center": v(707.11, 167.31) * mm, "radius": 3.18 * mm});
            skCircle(sketch, "E110.5.1.0", {"center": v(689.89, 446.71) * mm, "radius": 3.18 * mm});
            skCircle(sketch, "E110.5.1.1", {"center": v(689.89, 416.89) * mm, "radius": 3.18 * mm});
            skCircle(sketch, "E110.5.1.2", {"center": v(707.11, 416.89) * mm, "radius": 3.18 * mm});
            skCircle(sketch, "E110.5.1.3", {"center": v(707.11, 446.71) * mm, "radius": 3.18 * mm});
            skCircle(sketch, "E110.5.2.0", {"center": v(689.89, 726.11) * mm, "radius": 3.18 * mm});
            skCircle(sketch, "E110.5.2.1", {"center": v(689.89, 696.29) * mm, "radius": 3.18 * mm});
            skCircle(sketch, "E110.5.2.2", {"center": v(707.11, 696.29) * mm, "radius": 3.18 * mm});
            skCircle(sketch, "E110.5.2.3", {"center": v(707.11, 726.11) * mm, "radius": 3.18 * mm});
            skLineSegment(sketch, "E110.direction1", {"start": v(-707.11, 137.49) * mm, "end": v(-427.71, 137.49) * mm, "construction": true});
            skLineSegment(sketch, "E110.direction2", {"start": v(-707.11, 137.49) * mm, "end": v(-707.11, 416.89) * mm, "construction": true});
            skSolve(sketch);
        }
        {
            var Q0;
            Q0 = qSketchRegion(id + "F16", true);
            extrude(context, id + "F17", {"entities" : qUnion([Q0]), "operationType" : NewBodyOperationType.REMOVE, "endBound" : BoundingType.THROUGH_ALL, "oppositeDirection" : true, "depth" : 25.4 * mm});
        }
        {
            var Q0;
            Q0=makeQuery(id+"F1.opExtrude","CAP_FACE",FACE,{"disambiguationData":[OSD([sQuery(id+"F0.wireOp",EDGE,"E0.bottom"),sQuery(id+"F0.wireOp",EDGE,"E0.top"),sQuery(id+"F0.wireOp",EDGE,"E0.left"),sQuery(id+"F0.wireOp",EDGE,"E0.right"),sQuery(id+"F0.wireOp",EDGE,"E1.filletArc"),sQuery(id+"F0.wireOp",EDGE,"E2.filletArc"),sQuery(id+"F0.wireOp",EDGE,"E3.filletArc"),sQuery(id+"F0.wireOp",EDGE,"E4.filletArc")])],"isStart":false});
            var sketch = newSketch(context, id + "F18", { "sketchPlane" : qUnion([Q0])});
            skLineSegment(sketch, "E111", {"start": v(-812.8, 647.7) * mm, "end": v(812.8, 647.7) * mm, "construction": true});
            skLineSegment(sketch, "E112", {"start": v(812.8, 266.7) * mm, "end": v(-812.8, 266.7) * mm, "construction": true});
            skLineSegment(sketch, "E113", {"start": v(-812.8, 266.7) * mm, "end": v(-812.8, 101.6) * mm, "construction": true});
            skLineSegment(sketch, "E114", {"start": v(-812.8, 101.6) * mm, "end": v(-647.7, 101.6) * mm, "construction": true});
            skLineSegment(sketch, "E115", {"start": v(-647.7, 101.6) * mm, "end": v(-647.7, 812.8) * mm, "construction": true});
            skLineSegment(sketch, "E116", {"start": v(-647.7, 812.8) * mm, "end": v(-812.8, 812.8) * mm, "construction": true});
            skLineSegment(sketch, "E117", {"start": v(-812.8, 812.8) * mm, "end": v(-812.8, 647.7) * mm, "construction": true});
            skLineSegment(sketch, "E118", {"start": v(812.8, 647.7) * mm, "end": v(812.8, 812.8) * mm, "construction": true});
            skLineSegment(sketch, "E119", {"start": v(812.8, 812.8) * mm, "end": v(647.7, 812.8) * mm, "construction": true});
            skLineSegment(sketch, "E120", {"start": v(647.7, 812.8) * mm, "end": v(647.7, 101.6) * mm, "construction": true});
            skLineSegment(sketch, "E121", {"start": v(647.7, 101.6) * mm, "end": v(812.8, 101.6) * mm, "construction": true});
            skLineSegment(sketch, "E122", {"start": v(812.8, 101.6) * mm, "end": v(812.8, 266.7) * mm, "construction": true});
            skPoint(sketch, "E123", {"position": v(-647.7, 647.7) * mm});
            skPoint(sketch, "E124", {"position": v(-647.7, 266.7) * mm});
            skPoint(sketch, "E125", {"position": v(647.7, 266.7) * mm});
            skPoint(sketch, "E126", {"position": v(647.7, 647.7) * mm});
            skCircle(sketch, "E127", {"center": v(812.8, 812.8) * mm, "radius": 3.18 * mm});
            skCircle(sketch, "E128", {"center": v(647.7, 647.7) * mm, "radius": 3.18 * mm});
            skCircle(sketch, "E129", {"center": v(647.7, 266.7) * mm, "radius": 3.18 * mm});
            skCircle(sketch, "E130", {"center": v(812.8, 101.6) * mm, "radius": 3.18 * mm});
            skCircle(sketch, "E131", {"center": v(-812.8, 101.6) * mm, "radius": 3.18 * mm});
            skCircle(sketch, "E132", {"center": v(-647.7, 266.7) * mm, "radius": 3.18 * mm});
            skCircle(sketch, "E133", {"center": v(-812.8, 812.8) * mm, "radius": 3.18 * mm});
            skCircle(sketch, "E134", {"center": v(-647.7, 647.7) * mm, "radius": 3.18 * mm});
            skLineSegment(sketch, "E135", {"start": v(-647.7, 812.8) * mm, "end": v(647.7, 812.8) * mm, "construction": true});
            skLineSegment(sketch, "E136", {"start": v(-647.7, 101.6) * mm, "end": v(647.7, 101.6) * mm, "construction": true});
            skLineSegment(sketch, "E137", {"start": v(0, 101.6) * mm, "end": v(0, 812.8) * mm, "construction": true});
            skCircle(sketch, "E138", {"center": v(25.4, 812.8) * mm, "radius": 3.18 * mm});
            skCircle(sketch, "E139", {"center": v(-25.4, 101.6) * mm, "radius": 3.18 * mm});
            skSolve(sketch);
        }
        {
            var Q0;
            Q0 = qSketchRegion(id + "F18", true);
            extrude(context, id + "F19", {"entities" : qUnion([Q0]), "operationType" : NewBodyOperationType.REMOVE, "endBound" : BoundingType.THROUGH_ALL, "oppositeDirection" : true, "depth" : 25.4 * mm});
        }
        {
            var Q0;
            Q0=makeQuery(id+"F1.opExtrude","CAP_FACE",FACE,{"disambiguationData":[OSD([sQuery(id+"F0.wireOp",EDGE,"E0.bottom"),sQuery(id+"F0.wireOp",EDGE,"E0.top"),sQuery(id+"F0.wireOp",EDGE,"E0.left"),sQuery(id+"F0.wireOp",EDGE,"E0.right"),sQuery(id+"F0.wireOp",EDGE,"E1.filletArc"),sQuery(id+"F0.wireOp",EDGE,"E2.filletArc"),sQuery(id+"F0.wireOp",EDGE,"E3.filletArc"),sQuery(id+"F0.wireOp",EDGE,"E4.filletArc")])],"isStart":false});
            var sketch = newSketch(context, id + "F20", { "sketchPlane" : qUnion([Q0])});
            skLineSegment(sketch, "E140.bottom", {"start": v(-60.8, 736.6) * mm, "end": v(-14.6, 736.6) * mm});
            skLineSegment(sketch, "E140.top", {"start": v(-60.8, 693.1) * mm, "end": v(-14.6, 693.1) * mm});
            skLineSegment(sketch, "E140.left", {"start": v(-62.7, 734.7) * mm, "end": v(-62.7, 695) * mm});
            skLineSegment(sketch, "E140.right", {"start": v(-12.7, 734.7) * mm, "end": v(-12.7, 695) * mm});
            skArc(sketch, "E141", {"start": v(-60.8, 736.6) * mm, "mid": v(-64.05, 737.95) * mm, "end": v(-62.7, 734.7) * mm});
            skArc(sketch, "E142", {"start": v(-62.7, 695) * mm, "mid": v(-64.05, 691.75) * mm, "end": v(-60.8, 693.1) * mm});
            skArc(sketch, "E143", {"start": v(-14.6, 693.1) * mm, "mid": v(-11.35, 691.75) * mm, "end": v(-12.7, 695) * mm});
            skArc(sketch, "E144", {"start": v(-12.7, 734.7) * mm, "mid": v(-11.35, 737.95) * mm, "end": v(-14.6, 736.6) * mm});
            skSolve(sketch);
        }
        {
            var Q0;
            Q0 = qSketchRegion(id + "F20", true);
            extrude(context, id + "F21", {"entities" : qUnion([Q0]), "operationType" : NewBodyOperationType.REMOVE, "endBound" : BoundingType.THROUGH_ALL, "oppositeDirection" : true, "depth" : 25.4 * mm});
        }
    });
